MODEL slx_38dcbebacd56
CONFIG AbsTol = auto
CONFIG FixedStep = 0.001
CONFIG MaxStep = auto
CONFIG MinStep = auto
CONFIG PostLoadFcn = , if any(exist('dsrtsu_mdlpostloadfcn', 'file') == [2, 3, 6]), try dsrtsu_mdlpostloadfcn('Execute', bdroot); catch fprintf('Error in PostLoadFcn (dsrtsu_mdlpostloadfcn) for model "%s":\n %s\n', bdroot, lasterr); end, end, 

CONFIG RelTol = 1e-3
CONFIG SampleTimeConstraint = Unconstrained
CONFIG Solver = ode1
CONFIG SolverMode = Auto
CONFIG SolverName = ode1
CONFIG StartTime = 0.0
CONFIG StopTime = Inf
BLOCK [Reference] DS2201ADC_B1  REF=rtilibm/DS2201/DS2201ADC_B1
  BoardNo = 1
  DSProperties = struct('RTI',struct('Version',uint32(1),'BlockType',struct('isSLSource',uint8(1),'isSLSink',uint8(0),'isHWSource',uint8(1),'isHWSink',uint8(0),'isSetup',uint8(0),'isInline',uint8(1),'isNonInline',uint8(0),'isInterrupt',uint8(0),'isChannelwise',uint8(0)),'IOBoardType','DS2201','UnitType','ADC','Identifier','ADCMUX','DialogType','ML','BlockSet','NONE','SlaveProcessor','NONE'))
  Diagnostics = AllowInheritedTsInSrc
  DialogFcn = gui2201adc
  Ports = [0, 5]
  SourceBlock = rtilibm/DS2201/DS2201ADC_B1
  SourceType = DS2201ADC
  UnitName = {'DS2201ADC_B'}
  UnitValues = { 1 }
  channelNo1 = [1 2 3 4]
  channelNo2 = [5 6 7 8]
  channelNo3 = [9 10]
  channelNo4 = -1
  channelNo5 = -1
BLOCK [Reference] DS2201DAC_B1  REF=rtilibm/DS2201/DS2201DAC_B1
  BoardNo = 1
  DSProperties = struct('RTI',struct('Version',uint32(1),'BlockType',struct('isSLSource',uint8(0),'isSLSink',uint8(1),'isHWSource',uint8(0),'isHWSink',uint8(1),'isSetup',uint8(0),'isInline',uint8(1),'isNonInline',uint8(0),'isInterrupt',uint8(0),'isChannelwise',uint8(0)),'IOBoardType','DS2201','UnitType','DAC','Identifier','DAC','DialogType','ML','BlockSet','NONE','SlaveProcessor','NONE'))
  Diagnostics = AllowInheritedTsInSrc
  DialogFcn = gui2201dac
  IOErrorMode = [0 0]
  InitValue = [0 0 0 0 0 0 0 0]
  Ports = [8]
  SourceBlock = rtilibm/DS2201/DS2201DAC_B1
  SourceType = DS2201DAC
  TermMode = [0 0 0 0 0 0 0 0]
  TermValue = [0 0 0 0 0 0 0 0]
  UnitName = {'DS2201DAC_B'}
  UnitValues = { 1 }
BLOCK [Reference] DS2201IN_B3  REF=rtilibm/DS2201/DS2201IN_B1
  BoardNo = 3
  ChannelNos = [1 2 3]
  DSProperties = struct('RTI',struct('Version',uint32(1),'BlockType',struct('isSLSource',uint8(1),'isSLSink',uint8(0),'isHWSource',uint8(1),'isHWSink',uint8(0),'isSetup',uint8(0),'isInline',uint8(1),'isNonInline',uint8(0),'isInterrupt',uint8(0),'isChannelwise',uint8(0)),'IOBoardType','DS2201','UnitType','BIT','Identifier','BITIN','DialogType','ML','BlockSet','NONE','SlaveProcessor','NONE'))
  DialogFcn = gui2201in
  Ports = [0, 1]
  SourceBlock = rtilibm/DS2201/DS2201IN_B1
  SourceType = DS2201IN
  UnitName = { 'DS2201IN_B' }
  UnitValues = { 3 }
BLOCK [DataStoreMemory] Data Store Memory
  DataStoreName = czuj_baz_os_1
  ReadBeforeWriteMsg = warning
  WriteAfterReadMsg = warning
  WriteAfterWriteMsg = warning
BLOCK [DataStoreMemory] Data Store Memory1
  DataStoreName = os2_zad
  ReadBeforeWriteMsg = warning
  WriteAfterReadMsg = warning
  WriteAfterWriteMsg = warning
BLOCK [DataStoreMemory] Data Store Memory10
  DataStoreName = czuj_baz_os_3
  ReadBeforeWriteMsg = warning
  WriteAfterReadMsg = warning
  WriteAfterWriteMsg = warning
BLOCK [DataStoreMemory] Data Store Memory11
  DataStoreName = Bazowanie_on
  OutDataTypeStr = double
  ReadBeforeWriteMsg = warning
  WriteAfterReadMsg = warning
  WriteAfterWriteMsg = warning
BLOCK [DataStoreMemory] Data Store Memory12
  DataStoreName = Bazowanie_off
  OutDataTypeStr = double
  ReadBeforeWriteMsg = warning
  WriteAfterReadMsg = warning
  WriteAfterWriteMsg = warning
BLOCK [DataStoreMemory] Data Store Memory13
  DataStoreName = reset_os_1
  ReadBeforeWriteMsg = warning
  WriteAfterReadMsg = warning
  WriteAfterWriteMsg = warning
BLOCK [DataStoreMemory] Data Store Memory14
  DataStoreName = reset_os_2
  ReadBeforeWriteMsg = warning
  WriteAfterReadMsg = warning
  WriteAfterWriteMsg = warning
BLOCK [DataStoreMemory] Data Store Memory15
  DataStoreName = reset_os_3
  ReadBeforeWriteMsg = warning
  WriteAfterReadMsg = warning
  WriteAfterWriteMsg = warning
BLOCK [DataStoreMemory] Data Store Memory16
  DataStoreName = predkosc_robocza
  ReadBeforeWriteMsg = warning
  WriteAfterReadMsg = warning
  WriteAfterWriteMsg = warning
BLOCK [DataStoreMemory] Data Store Memory17
  DataStoreName = wpolczynnik_predkosci_roboczej
  ReadBeforeWriteMsg = warning
  WriteAfterReadMsg = warning
  WriteAfterWriteMsg = warning
BLOCK [DataStoreMemory] Data Store Memory2
  DataStoreName = os3_zad
  ReadBeforeWriteMsg = warning
  WriteAfterReadMsg = warning
  WriteAfterWriteMsg = warning
BLOCK [DataStoreMemory] Data Store Memory3
  DataStoreName = os4_zad
  ReadBeforeWriteMsg = warning
  WriteAfterReadMsg = warning
  WriteAfterWriteMsg = warning
BLOCK [DataStoreMemory] Data Store Memory4
  DataStoreName = os5_zad
  ReadBeforeWriteMsg = warning
  WriteAfterReadMsg = warning
  WriteAfterWriteMsg = warning
BLOCK [DataStoreMemory] Data Store Memory5
  DataStoreName = os2_panel
  ReadBeforeWriteMsg = warning
  WriteAfterReadMsg = warning
  WriteAfterWriteMsg = warning
BLOCK [DataStoreMemory] Data Store Memory6
  DataStoreName = os3_panel
  ReadBeforeWriteMsg = warning
  WriteAfterReadMsg = warning
  WriteAfterWriteMsg = warning
BLOCK [DataStoreMemory] Data Store Memory7
  DataStoreName = os4_panel
  ReadBeforeWriteMsg = warning
  WriteAfterReadMsg = warning
  WriteAfterWriteMsg = warning
BLOCK [DataStoreMemory] Data Store Memory8
  DataStoreName = os5_panel
  ReadBeforeWriteMsg = warning
  WriteAfterReadMsg = warning
  WriteAfterWriteMsg = warning
BLOCK [DataStoreMemory] Data Store Memory9
  DataStoreName = czuj_baz_os_2
  ReadBeforeWriteMsg = warning
  WriteAfterReadMsg = warning
  WriteAfterWriteMsg = warning
BLOCK [DataStoreRead] Data Store Read
  DataStoreName = os1_zad
  Ports = [0, 1]
BLOCK [DataStoreRead] Data Store Read1
  DataStoreName = os2_zad
  Ports = [0, 1]
BLOCK [DataStoreRead] Data Store Read10
  DataStoreName = czuj_baz_os_1
  Ports = [0, 1]
BLOCK [DataStoreRead] Data Store Read11
  DataStoreName = reset_os_3
  Ports = [0, 1]
BLOCK [DataStoreRead] Data Store Read12
  DataStoreName = Bazowanie_off
  Ports = [0, 1]
BLOCK [DataStoreRead] Data Store Read13
  DataStoreName = reset_os_2
  Ports = [0, 1]
BLOCK [DataStoreRead] Data Store Read14
  DataStoreName = reset_os_1
  Ports = [0, 1]
BLOCK [DataStoreRead] Data Store Read15
  DataStoreName = predkosc_robocza
  Ports = [0, 1]
BLOCK [DataStoreRead] Data Store Read16
  DataStoreName = wpolczynnik_predkosci_roboczej
  Ports = [0, 1]
BLOCK [DataStoreRead] Data Store Read2
  DataStoreName = os3_zad
  Ports = [0, 1]
BLOCK [DataStoreRead] Data Store Read3
  DataStoreName = os4_zad
  Ports = [0, 1]
BLOCK [DataStoreRead] Data Store Read4
  DataStoreName = os5_zad
  Ports = [0, 1]
BLOCK [DataStoreRead] Data Store Read5
  DataStoreName = os1_panel
  Ports = [0, 1]
BLOCK [DataStoreRead] Data Store Read6
  DataStoreName = os2_panel
  Ports = [0, 1]
BLOCK [DataStoreRead] Data Store Read7
  DataStoreName = os3_panel
  Ports = [0, 1]
BLOCK [DataStoreRead] Data Store Read8
  DataStoreName = os4_panel
  Ports = [0, 1]
BLOCK [DataStoreRead] Data Store Read9
  DataStoreName = os5_panel
  Ports = [0, 1]
BLOCK [DataStoreWrite] Data Store Write
  DataStoreName = os1_zad
  Ports = [1]
BLOCK [DataStoreWrite] Data Store Write1
  DataStoreName = os2_zad
  Ports = [1]
BLOCK [DataStoreWrite] Data Store Write2
  DataStoreName = os3_zad
  Ports = [1]
BLOCK [DataStoreWrite] Data Store Write3
  DataStoreName = os4_zad
  Ports = [1]
BLOCK [DataStoreWrite] Data Store Write4
  DataStoreName = os5_zad
  Ports = [1]
BLOCK [DataStoreWrite] Data Store Write5
  DataStoreName = czuj_baz_os_1
  Ports = [1]
BLOCK [DataStoreWrite] Data Store Write6
  DataStoreName = czuj_baz_os_2
  Ports = [1]
BLOCK [DataStoreWrite] Data Store Write7
  DataStoreName = czuj_baz_os_3
  Ports = [1]
BLOCK [DataStoreWrite] Data Store Write8
  DataStoreName = wpolczynnik_predkosci_roboczej
  Ports = [1]
BLOCK [Demux] Demux
  DisplayOption = bar
  Outputs = 2
  Ports = [1, 2]
BLOCK [Demux] Demux1
  DisplayOption = bar
  Outputs = 2
  Ports = [1, 2]
BLOCK [Demux] Demux2
  DisplayOption = bar
  Outputs = 3
  Ports = [1, 3]
BLOCK [From] From
  GotoTag = os1
  TagVisibility = global
BLOCK [From] From1
  GotoTag = os2
  TagVisibility = global
BLOCK [From] From2
  GotoTag = os3
  TagVisibility = global
BLOCK [From] From3
  GotoTag = os4
  TagVisibility = global
BLOCK [From] From4
  GotoTag = os5
  TagVisibility = global
BLOCK [Gain] Gain
  Gain = 0.01
  OutDataTypeStr = Inherit: Inherit via internal rule
  ParamDataTypeStr = Inherit: Inherit via internal rule
  SaturateOnIntegerOverflow = off
BLOCK [Goto] Goto
  GotoTag = os1
  TagVisibility = global
BLOCK [Goto] Goto1
  GotoTag = os2
  TagVisibility = global
BLOCK [Goto] Goto2
  GotoTag = os3
  TagVisibility = global
BLOCK [Goto] Goto3
  GotoTag = os4
  TagVisibility = global
BLOCK [Goto] Goto4
  GotoTag = os5
  TagVisibility = global
BLOCK [Ground] Ground
BLOCK [Ground] Ground1
BLOCK [Ground] Ground2
BLOCK [SubSystem] Moduł sprawdzający czy wpisana pozycja dla ruchu, może być wartością zadaną dla regulatorów P, praz podana na elementy wykonawcze2
  Ports = [5, 5]
  RequestExecContextInheritance = off
BLOCK [Abs] Moduł sprawdzający czy wpisana pozycja dla ruchu, może być wartością zadaną dla regulatorów P, praz podana na elementy wykonawcze2/Abs
  SaturateOnIntegerOverflow = off
BLOCK [Abs] Moduł sprawdzający czy wpisana pozycja dla ruchu, może być wartością zadaną dla regulatorów P, praz podana na elementy wykonawcze2/Abs1
  SaturateOnIntegerOverflow = off
BLOCK [Abs] Moduł sprawdzający czy wpisana pozycja dla ruchu, może być wartością zadaną dla regulatorów P, praz podana na elementy wykonawcze2/Abs2
  SaturateOnIntegerOverflow = off
BLOCK [Constant] Moduł sprawdzający czy wpisana pozycja dla ruchu, może być wartością zadaną dla regulatorów P, praz podana na elementy wykonawcze2/Constant
  Value = 160
BLOCK [Constant] Moduł sprawdzający czy wpisana pozycja dla ruchu, może być wartością zadaną dla regulatorów P, praz podana na elementy wykonawcze2/Constant1
BLOCK [Constant] Moduł sprawdzający czy wpisana pozycja dla ruchu, może być wartością zadaną dla regulatorów P, praz podana na elementy wykonawcze2/Constant10
BLOCK [Constant] Moduł sprawdzający czy wpisana pozycja dla ruchu, może być wartością zadaną dla regulatorów P, praz podana na elementy wykonawcze2/Constant11
BLOCK [Constant] Moduł sprawdzający czy wpisana pozycja dla ruchu, może być wartością zadaną dla regulatorów P, praz podana na elementy wykonawcze2/Constant12
  Value = 25
BLOCK [Constant] Moduł sprawdzający czy wpisana pozycja dla ruchu, może być wartością zadaną dla regulatorów P, praz podana na elementy wykonawcze2/Constant13
BLOCK [Constant] Moduł sprawdzający czy wpisana pozycja dla ruchu, może być wartością zadaną dla regulatorów P, praz podana na elementy wykonawcze2/Constant14
  Value = 0
BLOCK [Constant] Moduł sprawdzający czy wpisana pozycja dla ruchu, może być wartością zadaną dla regulatorów P, praz podana na elementy wykonawcze2/Constant15
  Value = 120
BLOCK [Constant] Moduł sprawdzający czy wpisana pozycja dla ruchu, może być wartością zadaną dla regulatorów P, praz podana na elementy wykonawcze2/Constant16
BLOCK [Constant] Moduł sprawdzający czy wpisana pozycja dla ruchu, może być wartością zadaną dla regulatorów P, praz podana na elementy wykonawcze2/Constant17
  Value = 25
BLOCK [Constant] Moduł sprawdzający czy wpisana pozycja dla ruchu, może być wartością zadaną dla regulatorów P, praz podana na elementy wykonawcze2/Constant18
BLOCK [Constant] Moduł sprawdzający czy wpisana pozycja dla ruchu, może być wartością zadaną dla regulatorów P, praz podana na elementy wykonawcze2/Constant19
  Value = 0
BLOCK [Constant] Moduł sprawdzający czy wpisana pozycja dla ruchu, może być wartością zadaną dla regulatorów P, praz podana na elementy wykonawcze2/Constant2
  Value = 0
BLOCK [Constant] Moduł sprawdzający czy wpisana pozycja dla ruchu, może być wartością zadaną dla regulatorów P, praz podana na elementy wykonawcze2/Constant20
  Value = 150
BLOCK [Constant] Moduł sprawdzający czy wpisana pozycja dla ruchu, może być wartością zadaną dla regulatorów P, praz podana na elementy wykonawcze2/Constant21
  Value = 40
BLOCK [Constant] Moduł sprawdzający czy wpisana pozycja dla ruchu, może być wartością zadaną dla regulatorów P, praz podana na elementy wykonawcze2/Constant22
  Value = 0
BLOCK [Constant] Moduł sprawdzający czy wpisana pozycja dla ruchu, może być wartością zadaną dla regulatorów P, praz podana na elementy wykonawcze2/Constant23
BLOCK [Constant] Moduł sprawdzający czy wpisana pozycja dla ruchu, może być wartością zadaną dla regulatorów P, praz podana na elementy wykonawcze2/Constant3
  Value = 40
BLOCK [Constant] Moduł sprawdzający czy wpisana pozycja dla ruchu, może być wartością zadaną dla regulatorów P, praz podana na elementy wykonawcze2/Constant4
BLOCK [Constant] Moduł sprawdzający czy wpisana pozycja dla ruchu, może być wartością zadaną dla regulatorów P, praz podana na elementy wykonawcze2/Constant5
  Value = 0
BLOCK [Constant] Moduł sprawdzający czy wpisana pozycja dla ruchu, może być wartością zadaną dla regulatorów P, praz podana na elementy wykonawcze2/Constant6
  Value = 25
BLOCK [Constant] Moduł sprawdzający czy wpisana pozycja dla ruchu, może być wartością zadaną dla regulatorów P, praz podana na elementy wykonawcze2/Constant7
BLOCK [Constant] Moduł sprawdzający czy wpisana pozycja dla ruchu, może być wartością zadaną dla regulatorów P, praz podana na elementy wykonawcze2/Constant8
  Value = 0
BLOCK [Constant] Moduł sprawdzający czy wpisana pozycja dla ruchu, może być wartością zadaną dla regulatorów P, praz podana na elementy wykonawcze2/Constant9
  Value = 40
BLOCK [DataStoreRead] Moduł sprawdzający czy wpisana pozycja dla ruchu, może być wartością zadaną dla regulatorów P, praz podana na elementy wykonawcze2/Data Store Read17
  DataStoreName = os1_zad
  Ports = [0, 1]
BLOCK [DataStoreRead] Moduł sprawdzający czy wpisana pozycja dla ruchu, może być wartością zadaną dla regulatorów P, praz podana na elementy wykonawcze2/Data Store Read18
  DataStoreName = os2_zad
  Ports = [0, 1]
BLOCK [DataStoreRead] Moduł sprawdzający czy wpisana pozycja dla ruchu, może być wartością zadaną dla regulatorów P, praz podana na elementy wykonawcze2/Data Store Read19
  DataStoreName = os3_zad
  Ports = [0, 1]
BLOCK [DataStoreRead] Moduł sprawdzający czy wpisana pozycja dla ruchu, może być wartością zadaną dla regulatorów P, praz podana na elementy wykonawcze2/Data Store Read20
  DataStoreName = os4_zad
  Ports = [0, 1]
BLOCK [DataStoreRead] Moduł sprawdzający czy wpisana pozycja dla ruchu, może być wartością zadaną dla regulatorów P, praz podana na elementy wykonawcze2/Data Store Read21
  DataStoreName = os5_zad
  Ports = [0, 1]
BLOCK [From] Moduł sprawdzający czy wpisana pozycja dla ruchu, może być wartością zadaną dla regulatorów P, praz podana na elementy wykonawcze2/From
  GotoTag = os_3_wpis
  TagVisibility = global
BLOCK [From] Moduł sprawdzający czy wpisana pozycja dla ruchu, może być wartością zadaną dla regulatorów P, praz podana na elementy wykonawcze2/From1
  GotoTag = os_2_wpis
  TagVisibility = global
BLOCK [From] Moduł sprawdzający czy wpisana pozycja dla ruchu, może być wartością zadaną dla regulatorów P, praz podana na elementy wykonawcze2/From2
  GotoTag = os_5_wpis
  TagVisibility = global
BLOCK [From] Moduł sprawdzający czy wpisana pozycja dla ruchu, może być wartością zadaną dla regulatorów P, praz podana na elementy wykonawcze2/From3
  GotoTag = os_2_wpis
  TagVisibility = global
BLOCK [From] Moduł sprawdzający czy wpisana pozycja dla ruchu, może być wartością zadaną dla regulatorów P, praz podana na elementy wykonawcze2/From4
  GotoTag = os_1_wpis
  TagVisibility = global
BLOCK [From] Moduł sprawdzający czy wpisana pozycja dla ruchu, może być wartością zadaną dla regulatorów P, praz podana na elementy wykonawcze2/From5
  GotoTag = os_4_wpis
  TagVisibility = global
BLOCK [From] Moduł sprawdzający czy wpisana pozycja dla ruchu, może być wartością zadaną dla regulatorów P, praz podana na elementy wykonawcze2/From6
  GotoTag = os_3_wpis
  TagVisibility = global
BLOCK [Goto] Moduł sprawdzający czy wpisana pozycja dla ruchu, może być wartością zadaną dla regulatorów P, praz podana na elementy wykonawcze2/Goto
  GotoTag = os_1_wpis
  TagVisibility = global
BLOCK [Goto] Moduł sprawdzający czy wpisana pozycja dla ruchu, może być wartością zadaną dla regulatorów P, praz podana na elementy wykonawcze2/Goto1
  GotoTag = os_2_wpis
  TagVisibility = global
BLOCK [Goto] Moduł sprawdzający czy wpisana pozycja dla ruchu, może być wartością zadaną dla regulatorów P, praz podana na elementy wykonawcze2/Goto2
  GotoTag = os_5_wpis
  TagVisibility = global
BLOCK [Goto] Moduł sprawdzający czy wpisana pozycja dla ruchu, może być wartością zadaną dla regulatorów P, praz podana na elementy wykonawcze2/Goto3
  GotoTag = os_3_wpis
  TagVisibility = global
BLOCK [Goto] Moduł sprawdzający czy wpisana pozycja dla ruchu, może być wartością zadaną dla regulatorów P, praz podana na elementy wykonawcze2/Goto4
  GotoTag = os_4_wpis
  TagVisibility = global
BLOCK [Logic] Moduł sprawdzający czy wpisana pozycja dla ruchu, może być wartością zadaną dla regulatorów P, praz podana na elementy wykonawcze2/Logical Operator
  AllPortsSameDT = off
  Ports = [2, 1]
BLOCK [Logic] Moduł sprawdzający czy wpisana pozycja dla ruchu, może być wartością zadaną dla regulatorów P, praz podana na elementy wykonawcze2/Logical Operator1
  AllPortsSameDT = off
  Ports = [2, 1]
BLOCK [Logic] Moduł sprawdzający czy wpisana pozycja dla ruchu, może być wartością zadaną dla regulatorów P, praz podana na elementy wykonawcze2/Logical Operator2
  AllPortsSameDT = off
  Ports = [2, 1]
BLOCK [Logic] Moduł sprawdzający czy wpisana pozycja dla ruchu, może być wartością zadaną dla regulatorów P, praz podana na elementy wykonawcze2/Logical Operator3
  AllPortsSameDT = off
  Inputs = 6
  Ports = [6, 1]
BLOCK [Sum] Moduł sprawdzający czy wpisana pozycja dla ruchu, może być wartością zadaną dla regulatorów P, praz podana na elementy wykonawcze2/Sum
  IconShape = round
  InputSameDT = off
  Inputs = |+-
  OutDataTypeStr = Inherit: Inherit via internal rule
  Ports = [2, 1]
  SaturateOnIntegerOverflow = off
BLOCK [Sum] Moduł sprawdzający czy wpisana pozycja dla ruchu, może być wartością zadaną dla regulatorów P, praz podana na elementy wykonawcze2/Sum1
  IconShape = round
  InputSameDT = off
  Inputs = |+-
  OutDataTypeStr = Inherit: Inherit via internal rule
  Ports = [2, 1]
  SaturateOnIntegerOverflow = off
BLOCK [Sum] Moduł sprawdzający czy wpisana pozycja dla ruchu, może być wartością zadaną dla regulatorów P, praz podana na elementy wykonawcze2/Sum2
  IconShape = round
  InputSameDT = off
  Inputs = |++
  OutDataTypeStr = Inherit: Inherit via internal rule
  Ports = [2, 1]
  SaturateOnIntegerOverflow = off
BLOCK [Sum] Moduł sprawdzający czy wpisana pozycja dla ruchu, może być wartością zadaną dla regulatorów P, praz podana na elementy wykonawcze2/Sum3
  IconShape = round
  InputSameDT = off
  Inputs = |+-
  OutDataTypeStr = Inherit: Inherit via internal rule
  Ports = [2, 1]
  SaturateOnIntegerOverflow = off
BLOCK [Sum] Moduł sprawdzający czy wpisana pozycja dla ruchu, może być wartością zadaną dla regulatorów P, praz podana na elementy wykonawcze2/Sum4
  IconShape = round
  InputSameDT = off
  Inputs = |++
  OutDataTypeStr = Inherit: Inherit via internal rule
  Ports = [2, 1]
  SaturateOnIntegerOverflow = off
BLOCK [Sum] Moduł sprawdzający czy wpisana pozycja dla ruchu, może być wartością zadaną dla regulatorów P, praz podana na elementy wykonawcze2/Sum5
  IconShape = round
  InputSameDT = off
  Inputs = |+-
  OutDataTypeStr = Inherit: Inherit via internal rule
  Ports = [2, 1]
  SaturateOnIntegerOverflow = off
BLOCK [Sum] Moduł sprawdzający czy wpisana pozycja dla ruchu, może być wartością zadaną dla regulatorów P, praz podana na elementy wykonawcze2/Sum6
  IconShape = round
  InputSameDT = off
  Inputs = |++
  OutDataTypeStr = Inherit: Inherit via internal rule
  Ports = [2, 1]
  SaturateOnIntegerOverflow = off
BLOCK [Sum] Moduł sprawdzający czy wpisana pozycja dla ruchu, może być wartością zadaną dla regulatorów P, praz podana na elementy wykonawcze2/Sum7
  IconShape = round
  InputSameDT = off
  Inputs = |+-
  OutDataTypeStr = Inherit: Inherit via internal rule
  Ports = [2, 1]
  SaturateOnIntegerOverflow = off
BLOCK [Sum] Moduł sprawdzający czy wpisana pozycja dla ruchu, może być wartością zadaną dla regulatorów P, praz podana na elementy wykonawcze2/Sum8
  IconShape = round
  InputSameDT = off
  Inputs = |+-
  OutDataTypeStr = Inherit: Inherit via internal rule
  Ports = [2, 1]
  SaturateOnIntegerOverflow = off
BLOCK [Sum] Moduł sprawdzający czy wpisana pozycja dla ruchu, może być wartością zadaną dla regulatorów P, praz podana na elementy wykonawcze2/Sum9
  IconShape = round
  InputSameDT = off
  Inputs = |+-
  OutDataTypeStr = Inherit: Inherit via internal rule
  Ports = [2, 1]
  SaturateOnIntegerOverflow = off
BLOCK [Switch] Moduł sprawdzający czy wpisana pozycja dla ruchu, może być wartością zadaną dla regulatorów P, praz podana na elementy wykonawcze2/Switch
  InputSameDT = off
  SaturateOnIntegerOverflow = off
BLOCK [Switch] Moduł sprawdzający czy wpisana pozycja dla ruchu, może być wartością zadaną dla regulatorów P, praz podana na elementy wykonawcze2/Switch1
  InputSameDT = off
  SaturateOnIntegerOverflow = off
BLOCK [Switch] Moduł sprawdzający czy wpisana pozycja dla ruchu, może być wartością zadaną dla regulatorów P, praz podana na elementy wykonawcze2/Switch10
  Criteria = u2 > Threshold
  InputSameDT = off
  SaturateOnIntegerOverflow = off
BLOCK [Switch] Moduł sprawdzający czy wpisana pozycja dla ruchu, może być wartością zadaną dla regulatorów P, praz podana na elementy wykonawcze2/Switch11
  Criteria = u2 > Threshold
  InputSameDT = off
  SaturateOnIntegerOverflow = off
BLOCK [Switch] Moduł sprawdzający czy wpisana pozycja dla ruchu, może być wartością zadaną dla regulatorów P, praz podana na elementy wykonawcze2/Switch12
  Criteria = u2 > Threshold
  InputSameDT = off
  SaturateOnIntegerOverflow = off
BLOCK [Switch] Moduł sprawdzający czy wpisana pozycja dla ruchu, może być wartością zadaną dla regulatorów P, praz podana na elementy wykonawcze2/Switch13
  Criteria = u2 > Threshold
  InputSameDT = off
  SaturateOnIntegerOverflow = off
BLOCK [Switch] Moduł sprawdzający czy wpisana pozycja dla ruchu, może być wartością zadaną dla regulatorów P, praz podana na elementy wykonawcze2/Switch2
  InputSameDT = off
  SaturateOnIntegerOverflow = off
BLOCK [Switch] Moduł sprawdzający czy wpisana pozycja dla ruchu, może być wartością zadaną dla regulatorów P, praz podana na elementy wykonawcze2/Switch3
  InputSameDT = off
  SaturateOnIntegerOverflow = off
BLOCK [Switch] Moduł sprawdzający czy wpisana pozycja dla ruchu, może być wartością zadaną dla regulatorów P, praz podana na elementy wykonawcze2/Switch4
  InputSameDT = off
  SaturateOnIntegerOverflow = off
BLOCK [Switch] Moduł sprawdzający czy wpisana pozycja dla ruchu, może być wartością zadaną dla regulatorów P, praz podana na elementy wykonawcze2/Switch5
  InputSameDT = off
  SaturateOnIntegerOverflow = off
BLOCK [Switch] Moduł sprawdzający czy wpisana pozycja dla ruchu, może być wartością zadaną dla regulatorów P, praz podana na elementy wykonawcze2/Switch6
  InputSameDT = off
  SaturateOnIntegerOverflow = off
BLOCK [Switch] Moduł sprawdzający czy wpisana pozycja dla ruchu, może być wartością zadaną dla regulatorów P, praz podana na elementy wykonawcze2/Switch7
  InputSameDT = off
  SaturateOnIntegerOverflow = off
BLOCK [Switch] Moduł sprawdzający czy wpisana pozycja dla ruchu, może być wartością zadaną dla regulatorów P, praz podana na elementy wykonawcze2/Switch8
  InputSameDT = off
  SaturateOnIntegerOverflow = off
BLOCK [Switch] Moduł sprawdzający czy wpisana pozycja dla ruchu, może być wartością zadaną dla regulatorów P, praz podana na elementy wykonawcze2/Switch9
  Criteria = u2 > Threshold
  InputSameDT = off
  SaturateOnIntegerOverflow = off
BLOCK [Inport] Moduł sprawdzający czy wpisana pozycja dla ruchu, może być wartością zadaną dla regulatorów P, praz podana na elementy wykonawcze2/os1_
  IconDisplay = Port number
BLOCK [Inport] Moduł sprawdzający czy wpisana pozycja dla ruchu, może być wartością zadaną dla regulatorów P, praz podana na elementy wykonawcze2/os2
  IconDisplay = Port number
  Port = 2
BLOCK [Inport] Moduł sprawdzający czy wpisana pozycja dla ruchu, może być wartością zadaną dla regulatorów P, praz podana na elementy wykonawcze2/os3
  IconDisplay = Port number
  Port = 3
BLOCK [Inport] Moduł sprawdzający czy wpisana pozycja dla ruchu, może być wartością zadaną dla regulatorów P, praz podana na elementy wykonawcze2/os4
  IconDisplay = Port number
  Port = 4
BLOCK [Inport] Moduł sprawdzający czy wpisana pozycja dla ruchu, może być wartością zadaną dla regulatorów P, praz podana na elementy wykonawcze2/os5
  IconDisplay = Port number
  Port = 5
BLOCK [Outport] Moduł sprawdzający czy wpisana pozycja dla ruchu, może być wartością zadaną dla regulatorów P, praz podana na elementy wykonawcze2/os_1
  IconDisplay = Port number
BLOCK [Outport] Moduł sprawdzający czy wpisana pozycja dla ruchu, może być wartością zadaną dla regulatorów P, praz podana na elementy wykonawcze2/os_2
  IconDisplay = Port number
  Port = 2
BLOCK [Outport] Moduł sprawdzający czy wpisana pozycja dla ruchu, może być wartością zadaną dla regulatorów P, praz podana na elementy wykonawcze2/os_3
  IconDisplay = Port number
  Port = 3
BLOCK [Outport] Moduł sprawdzający czy wpisana pozycja dla ruchu, może być wartością zadaną dla regulatorów P, praz podana na elementy wykonawcze2/os_4
  IconDisplay = Port number
  Port = 4
BLOCK [Outport] Moduł sprawdzający czy wpisana pozycja dla ruchu, może być wartością zadaną dla regulatorów P, praz podana na elementy wykonawcze2/os_5
  IconDisplay = Port number
  Port = 5
BLOCK [SubSystem] Position 1
  Ports = [2, 1]
  RequestExecContextInheritance = off
BLOCK [SubSystem] Position 1/Filters 1
  Ports = [1, 2]
  RequestExecContextInheritance = off
  ShowPortLabels = none
BLOCK [SubSystem] Position 1/Filters 1/Analog Butterworth LP Filter
  Ports = [1, 1]
  RequestExecContextInheritance = off
BLOCK [ZeroPole] Position 1/Filters 1/Analog Butterworth LP Filter/Analog Butterworth LP Filter
  Gain = k
  Poles = p
  Zeros = z
BLOCK [Inport] Position 1/Filters 1/Analog Butterworth LP Filter/In1
  IconDisplay = Port number
BLOCK [Outport] Position 1/Filters 1/Analog Butterworth LP Filter/Out1
  IconDisplay = Port number
BLOCK [SubSystem] Position 1/Filters 1/Analog Butterworth LP Filter1
  Ports = [1, 1]
  RequestExecContextInheritance = off
BLOCK [ZeroPole] Position 1/Filters 1/Analog Butterworth LP Filter1/Analog Butterworth LP Filter1
  Gain = k
  Poles = p
  Zeros = z
BLOCK [Inport] Position 1/Filters 1/Analog Butterworth LP Filter1/In1
  IconDisplay = Port number
BLOCK [Outport] Position 1/Filters 1/Analog Butterworth LP Filter1/Out1
  IconDisplay = Port number
BLOCK [Outport] Position 1/Filters 1/Cos
  IconDisplay = Port number
  Port = 2
BLOCK [Demux] Position 1/Filters 1/Demux
  Outputs = 2
  Ports = [1, 2]
BLOCK [Outport] Position 1/Filters 1/Sin
  IconDisplay = Port number
BLOCK [Inport] Position 1/Filters 1/Sin && Cos
  IconDisplay = Port number
BLOCK [Outport] Position 1/Out1
  IconDisplay = Port number
BLOCK [SubSystem] Position 1/Position Calculation 1
  Ports = [3, 1]
  RequestExecContextInheritance = off
  ShowPortLabels = none
BLOCK [Fcn] Position 1/Position Calculation 1/Atan2
  Expr = atan2(u[1],u[2])
BLOCK [Gain] Position 1/Position Calculation 1/Conversion Rad to Deg
  Gain = 180/pi
BLOCK [Gain] Position 1/Position Calculation 1/Conversion Rotation to Angle
  Gain = 2*pi
BLOCK [Inport] Position 1/Position Calculation 1/Cos
  IconDisplay = Port number
  Port = 2
BLOCK [DeadZone] Position 1/Position Calculation 1/Dead Zone
  LowerValue = -5000
  UpperValue = 5000
BLOCK [Derivative] Position 1/Position Calculation 1/Derivative
BLOCK [Gain] Position 1/Position Calculation 1/Gear
  Gain = 6.33e-3
BLOCK [Switch] Position 1/Position Calculation 1/Init Angle
  Threshold = 1
BLOCK [Memory] Position 1/Position Calculation 1/Memory
BLOCK [Memory] Position 1/Position Calculation 1/Memory1
BLOCK [Mux] Position 1/Position Calculation 1/Mux
  Inputs = 2
  Ports = [2, 1]
BLOCK [Outport] Position 1/Position Calculation 1/Position
  IconDisplay = Port number
BLOCK [Product] Position 1/Position Calculation 1/Product
  Ports = [2, 1]
BLOCK [Inport] Position 1/Position Calculation 1/Reset (Impulse)
  IconDisplay = Port number
  Port = 3
BLOCK [Saturate] Position 1/Position Calculation 1/Saturation
  InputPortMap = u0
  LowerLimit = -1
  Ports = [1, 1]
  UpperLimit = 1
BLOCK [Inport] Position 1/Position Calculation 1/Sin
  IconDisplay = Port number
BLOCK [Sum] Position 1/Position Calculation 1/Sum
  Inputs = +-
  Ports = [2, 1]
BLOCK [Sum] Position 1/Position Calculation 1/Sum1
  Inputs = ++-
  Ports = [3, 1]
BLOCK [Inport] Position 1/Reset 1
  IconDisplay = Port number
  Port = 2
BLOCK [Inport] Position 1/Sin && Cos1
  IconDisplay = Port number
BLOCK [SubSystem] Position 2
  Ports = [2, 1]
  RequestExecContextInheritance = off
BLOCK [SubSystem] Position 2/Filters 2
  Ports = [1, 2]
  RequestExecContextInheritance = off
  ShowPortLabels = none
BLOCK [SubSystem] Position 2/Filters 2/Analog Butterworth LP Filter
  Ports = [1, 1]
  RequestExecContextInheritance = off
BLOCK [ZeroPole] Position 2/Filters 2/Analog Butterworth LP Filter/Analog Butterworth LP Filter
  Gain = k
  Poles = p
  Zeros = z
BLOCK [Inport] Position 2/Filters 2/Analog Butterworth LP Filter/In1
  IconDisplay = Port number
BLOCK [Outport] Position 2/Filters 2/Analog Butterworth LP Filter/Out1
  IconDisplay = Port number
BLOCK [SubSystem] Position 2/Filters 2/Analog Butterworth LP Filter1
  Ports = [1, 1]
  RequestExecContextInheritance = off
BLOCK [ZeroPole] Position 2/Filters 2/Analog Butterworth LP Filter1/Analog Butterworth LP Filter1
  Gain = k
  Poles = p
  Zeros = z
BLOCK [Inport] Position 2/Filters 2/Analog Butterworth LP Filter1/In1
  IconDisplay = Port number
BLOCK [Outport] Position 2/Filters 2/Analog Butterworth LP Filter1/Out1
  IconDisplay = Port number
BLOCK [Outport] Position 2/Filters 2/Cos
  IconDisplay = Port number
  Port = 2
BLOCK [Demux] Position 2/Filters 2/Demux
  Outputs = 2
  Ports = [1, 2]
BLOCK [Outport] Position 2/Filters 2/Sin
  IconDisplay = Port number
BLOCK [Inport] Position 2/Filters 2/Sin && Cos
  IconDisplay = Port number
BLOCK [Outport] Position 2/Out1
  IconDisplay = Port number
BLOCK [SubSystem] Position 2/Position Calculation 2
  Ports = [3, 1]
  RequestExecContextInheritance = off
  ShowPortLabels = none
BLOCK [Fcn] Position 2/Position Calculation 2/Atan2
  Expr = atan2(u[1],u[2])
BLOCK [Gain] Position 2/Position Calculation 2/Conversion Rad to Deg
  Gain = 180/pi
BLOCK [Gain] Position 2/Position Calculation 2/Conversion Rotation to Angle
  Gain = 2*pi
BLOCK [Inport] Position 2/Position Calculation 2/Cos
  IconDisplay = Port number
  Port = 2
BLOCK [DeadZone] Position 2/Position Calculation 2/Dead Zone
  LowerValue = -5000
  UpperValue = 5000
BLOCK [Derivative] Position 2/Position Calculation 2/Derivative
BLOCK [Gain] Position 2/Position Calculation 2/Gear
  Gain = 6.37e-3
BLOCK [Switch] Position 2/Position Calculation 2/Init Angle
  Threshold = 1
BLOCK [Memory] Position 2/Position Calculation 2/Memory
BLOCK [Memory] Position 2/Position Calculation 2/Memory1
BLOCK [Mux] Position 2/Position Calculation 2/Mux
  Inputs = 2
  Ports = [2, 1]
BLOCK [Outport] Position 2/Position Calculation 2/Position
  IconDisplay = Port number
BLOCK [Product] Position 2/Position Calculation 2/Product
  Ports = [2, 1]
BLOCK [Inport] Position 2/Position Calculation 2/Reset (Impulse)
  IconDisplay = Port number
  Port = 3
BLOCK [Saturate] Position 2/Position Calculation 2/Saturation
  InputPortMap = u0
  LowerLimit = -1
  Ports = [1, 1]
  UpperLimit = 1
BLOCK [Inport] Position 2/Position Calculation 2/Sin
  IconDisplay = Port number
BLOCK [Sum] Position 2/Position Calculation 2/Sum
  Inputs = +-
  Ports = [2, 1]
BLOCK [Sum] Position 2/Position Calculation 2/Sum1
  Inputs = ++-
  Ports = [3, 1]
BLOCK [Inport] Position 2/Reset 2
  IconDisplay = Port number
  Port = 2
BLOCK [Inport] Position 2/Sin && Cos2
  IconDisplay = Port number
BLOCK [SubSystem] Position 3
  Ports = [2, 1]
  RequestExecContextInheritance = off
BLOCK [SubSystem] Position 3/Filters 3
  Ports = [1, 2]
  RequestExecContextInheritance = off
  ShowPortLabels = none
BLOCK [SubSystem] Position 3/Filters 3/Analog Butterworth LP Filter
  Ports = [1, 1]
  RequestExecContextInheritance = off
BLOCK [ZeroPole] Position 3/Filters 3/Analog Butterworth LP Filter/Analog Butterworth LP Filter
  Gain = k
  Poles = p
  Zeros = z
BLOCK [Inport] Position 3/Filters 3/Analog Butterworth LP Filter/In1
  IconDisplay = Port number
BLOCK [Outport] Position 3/Filters 3/Analog Butterworth LP Filter/Out1
  IconDisplay = Port number
BLOCK [SubSystem] Position 3/Filters 3/Analog Butterworth LP Filter1
  Ports = [1, 1]
  RequestExecContextInheritance = off
BLOCK [ZeroPole] Position 3/Filters 3/Analog Butterworth LP Filter1/Analog Butterworth LP Filter1
  Gain = k
  Poles = p
  Zeros = z
BLOCK [Inport] Position 3/Filters 3/Analog Butterworth LP Filter1/In1
  IconDisplay = Port number
BLOCK [Outport] Position 3/Filters 3/Analog Butterworth LP Filter1/Out1
  IconDisplay = Port number
BLOCK [Outport] Position 3/Filters 3/Cos
  IconDisplay = Port number
  Port = 2
BLOCK [Demux] Position 3/Filters 3/Demux
  Outputs = 2
  Ports = [1, 2]
BLOCK [Outport] Position 3/Filters 3/Sin
  IconDisplay = Port number
BLOCK [Inport] Position 3/Filters 3/Sin && Cos
  IconDisplay = Port number
BLOCK [Outport] Position 3/Out1
  IconDisplay = Port number
BLOCK [SubSystem] Position 3/Position Calculation 3
  Ports = [3, 1]
  RequestExecContextInheritance = off
  ShowPortLabels = none
BLOCK [Fcn] Position 3/Position Calculation 3/Atan2
  Expr = atan2(u[1],u[2])
BLOCK [Gain] Position 3/Position Calculation 3/Conversion Rad to Deg
  Gain = 180/pi
BLOCK [Gain] Position 3/Position Calculation 3/Conversion Rotation to Angle
  Gain = 2*pi
BLOCK [Inport] Position 3/Position Calculation 3/Cos
  IconDisplay = Port number
  Port = 2
BLOCK [DeadZone] Position 3/Position Calculation 3/Dead Zone
  LowerValue = -5000
  UpperValue = 5000
BLOCK [Derivative] Position 3/Position Calculation 3/Derivative
BLOCK [Gain] Position 3/Position Calculation 3/Gear
  Gain = 6.33e-3
BLOCK [Switch] Position 3/Position Calculation 3/Init Angle
  Threshold = 1
BLOCK [Memory] Position 3/Position Calculation 3/Memory
BLOCK [Memory] Position 3/Position Calculation 3/Memory1
BLOCK [Mux] Position 3/Position Calculation 3/Mux
  Inputs = 2
  Ports = [2, 1]
BLOCK [Outport] Position 3/Position Calculation 3/Position
  IconDisplay = Port number
BLOCK [Product] Position 3/Position Calculation 3/Product
  Ports = [2, 1]
BLOCK [Inport] Position 3/Position Calculation 3/Reset (Impulse)
  IconDisplay = Port number
  Port = 3
BLOCK [Saturate] Position 3/Position Calculation 3/Saturation
  InputPortMap = u0
  LowerLimit = -1
  Ports = [1, 1]
  UpperLimit = 1
BLOCK [Inport] Position 3/Position Calculation 3/Sin
  IconDisplay = Port number
BLOCK [Sum] Position 3/Position Calculation 3/Sum
  Inputs = +-
  Ports = [2, 1]
BLOCK [Sum] Position 3/Position Calculation 3/Sum1
  Inputs = ++-
  Ports = [3, 1]
BLOCK [Inport] Position 3/Reset 3
  IconDisplay = Port number
  Port = 2
BLOCK [Inport] Position 3/Sin && Cos3
  IconDisplay = Port number
BLOCK [SubSystem] Position 4
  Ports = [2, 1]
  RequestExecContextInheritance = off
BLOCK [SubSystem] Position 4/Filters 4
  Ports = [1, 2]
  RequestExecContextInheritance = off
  ShowPortLabels = none
BLOCK [SubSystem] Position 4/Filters 4/Analog Butterworth LP Filter
  Ports = [1, 1]
  RequestExecContextInheritance = off
BLOCK [ZeroPole] Position 4/Filters 4/Analog Butterworth LP Filter/Analog Butterworth LP Filter
  Gain = k
  Poles = p
  Zeros = z
BLOCK [Inport] Position 4/Filters 4/Analog Butterworth LP Filter/In1
  IconDisplay = Port number
BLOCK [Outport] Position 4/Filters 4/Analog Butterworth LP Filter/Out1
  IconDisplay = Port number
BLOCK [SubSystem] Position 4/Filters 4/Analog Butterworth LP Filter1
  Ports = [1, 1]
  RequestExecContextInheritance = off
BLOCK [ZeroPole] Position 4/Filters 4/Analog Butterworth LP Filter1/Analog Butterworth LP Filter1
  Gain = k
  Poles = p
  Zeros = z
BLOCK [Inport] Position 4/Filters 4/Analog Butterworth LP Filter1/In1
  IconDisplay = Port number
BLOCK [Outport] Position 4/Filters 4/Analog Butterworth LP Filter1/Out1
  IconDisplay = Port number
BLOCK [Outport] Position 4/Filters 4/Cos
  IconDisplay = Port number
  Port = 2
BLOCK [Demux] Position 4/Filters 4/Demux
  Outputs = 2
  Ports = [1, 2]
BLOCK [Outport] Position 4/Filters 4/Sin
  IconDisplay = Port number
BLOCK [Inport] Position 4/Filters 4/Sin && Cos
  IconDisplay = Port number
BLOCK [Outport] Position 4/Out1
  IconDisplay = Port number
BLOCK [SubSystem] Position 4/Position Calculation 4
  Ports = [3, 1]
  RequestExecContextInheritance = off
  ShowPortLabels = none
BLOCK [Fcn] Position 4/Position Calculation 4/Atan2
  Expr = atan2(u[1],u[2])
BLOCK [Gain] Position 4/Position Calculation 4/Conversion Rad to Deg
  Gain = 180/pi
BLOCK [Gain] Position 4/Position Calculation 4/Conversion Rotation to Angle
  Gain = 2*pi
BLOCK [Inport] Position 4/Position Calculation 4/Cos
  IconDisplay = Port number
  Port = 2
BLOCK [DeadZone] Position 4/Position Calculation 4/Dead Zone
  LowerValue = -5000
  UpperValue = 5000
BLOCK [Derivative] Position 4/Position Calculation 4/Derivative
BLOCK [Gain] Position 4/Position Calculation 4/Gear
  Gain = 7.87e-3
BLOCK [Switch] Position 4/Position Calculation 4/Init Angle
  Threshold = 1
BLOCK [Memory] Position 4/Position Calculation 4/Memory
BLOCK [Memory] Position 4/Position Calculation 4/Memory1
BLOCK [Mux] Position 4/Position Calculation 4/Mux
  Inputs = 2
  Ports = [2, 1]
BLOCK [Outport] Position 4/Position Calculation 4/Position
  IconDisplay = Port number
BLOCK [Product] Position 4/Position Calculation 4/Product
  Ports = [2, 1]
BLOCK [Inport] Position 4/Position Calculation 4/Reset (Impulse)
  IconDisplay = Port number
  Port = 3
BLOCK [Saturate] Position 4/Position Calculation 4/Saturation
  InputPortMap = u0
  LowerLimit = -1
  Ports = [1, 1]
  UpperLimit = 1
BLOCK [Inport] Position 4/Position Calculation 4/Sin
  IconDisplay = Port number
BLOCK [Sum] Position 4/Position Calculation 4/Sum
  Inputs = +-
  Ports = [2, 1]
BLOCK [Sum] Position 4/Position Calculation 4/Sum1
  Inputs = ++-
  Ports = [3, 1]
BLOCK [Inport] Position 4/Reset 4
  IconDisplay = Port number
  Port = 2
BLOCK [Inport] Position 4/Sin && Cos4
  IconDisplay = Port number
BLOCK [SubSystem] Position 5
  Ports = [2, 1]
  RequestExecContextInheritance = off
BLOCK [SubSystem] Position 5/Filters 5
  Ports = [1, 2]
  RequestExecContextInheritance = off
  ShowPortLabels = none
BLOCK [SubSystem] Position 5/Filters 5/Analog Butterworth LP Filter
  Ports = [1, 1]
  RequestExecContextInheritance = off
BLOCK [ZeroPole] Position 5/Filters 5/Analog Butterworth LP Filter/Analog Butterworth LP Filter
  Gain = k
  Poles = p
  Zeros = z
BLOCK [Inport] Position 5/Filters 5/Analog Butterworth LP Filter/In1
  IconDisplay = Port number
BLOCK [Outport] Position 5/Filters 5/Analog Butterworth LP Filter/Out1
  IconDisplay = Port number
BLOCK [SubSystem] Position 5/Filters 5/Analog Butterworth LP Filter1
  Ports = [1, 1]
  RequestExecContextInheritance = off
BLOCK [ZeroPole] Position 5/Filters 5/Analog Butterworth LP Filter1/Analog Butterworth LP Filter1
  Gain = k
  Poles = p
  Zeros = z
BLOCK [Inport] Position 5/Filters 5/Analog Butterworth LP Filter1/In1
  IconDisplay = Port number
BLOCK [Outport] Position 5/Filters 5/Analog Butterworth LP Filter1/Out1
  IconDisplay = Port number
BLOCK [Outport] Position 5/Filters 5/Cos
  IconDisplay = Port number
  Port = 2
BLOCK [Demux] Position 5/Filters 5/Demux
  Outputs = 2
  Ports = [1, 2]
BLOCK [Outport] Position 5/Filters 5/Sin
  IconDisplay = Port number
BLOCK [Inport] Position 5/Filters 5/Sin && Cos
  IconDisplay = Port number
BLOCK [Outport] Position 5/Out1
  IconDisplay = Port number
BLOCK [SubSystem] Position 5/Position Calculation 5
  Ports = [3, 1]
  RequestExecContextInheritance = off
  ShowPortLabels = none
BLOCK [Fcn] Position 5/Position Calculation 5/Atan2
  Expr = atan2(u[1],u[2])
BLOCK [Gain] Position 5/Position Calculation 5/Conversion Rad to Deg
  Gain = 180/pi
BLOCK [Gain] Position 5/Position Calculation 5/Conversion Rotation to Angle
  Gain = 2*pi
BLOCK [Inport] Position 5/Position Calculation 5/Cos
  IconDisplay = Port number
  Port = 2
BLOCK [DeadZone] Position 5/Position Calculation 5/Dead Zone
  LowerValue = -5000
  UpperValue = 5000
BLOCK [Derivative] Position 5/Position Calculation 5/Derivative
BLOCK [Gain] Position 5/Position Calculation 5/Gear
  Gain = 1.32e-2
BLOCK [Switch] Position 5/Position Calculation 5/Init Angle
  Threshold = 1
BLOCK [Memory] Position 5/Position Calculation 5/Memory
BLOCK [Memory] Position 5/Position Calculation 5/Memory1
BLOCK [Mux] Position 5/Position Calculation 5/Mux
  Inputs = 2
  Ports = [2, 1]
BLOCK [Outport] Position 5/Position Calculation 5/Position
  IconDisplay = Port number
BLOCK [Product] Position 5/Position Calculation 5/Product
  Ports = [2, 1]
BLOCK [Inport] Position 5/Position Calculation 5/Reset (Impulse)
  IconDisplay = Port number
  Port = 3
BLOCK [Saturate] Position 5/Position Calculation 5/Saturation
  InputPortMap = u0
  LowerLimit = -1
  Ports = [1, 1]
  UpperLimit = 1
BLOCK [Inport] Position 5/Position Calculation 5/Sin
  IconDisplay = Port number
BLOCK [Sum] Position 5/Position Calculation 5/Sum
  Inputs = +-
  Ports = [2, 1]
BLOCK [Sum] Position 5/Position Calculation 5/Sum1
  Inputs = ++-
  Ports = [3, 1]
BLOCK [Inport] Position 5/Reset 5
  IconDisplay = Port number
  Port = 2
BLOCK [Inport] Position 5/Sin && Cos5
  IconDisplay = Port number
BLOCK [SubSystem] RTI Data
  CopyFcn = if exist('rtidc'), try,  rtidc('DataHostBlockClbCopy', gcbh); catch, disp(['Warning: ''CopyFcn'' for RTI Data block failed: ' lasterr]); end, end,
  DeleteFcn = if exist('rtidc'), try,  rtidc('DataHostBlockClbDelete', gcbh); catch, disp(['Warning: ''DeleteFcn'' for RTI Data block failed: ' lasterr]); end, end,
  LoadFcn = if exist('rtidc'), try,  rtidc('DataHostBlockClbLoad', gcbh); catch, disp(['Warning: ''LoadFcn'' for RTI Data block failed: ' lasterr]); end, end,
  ModelCloseFcn = if exist('rtidc'), try,  rtidc('DataHostBlockClbModelClose', gcbh); catch, disp(['Warning: ''ModelCloseFcn'' for RTI Data block failed: ' lasterr]); end, end,
  NameChangeFcn = if exist('rtidc'), try,  rtidc('DataHostBlockClbNameChange', gcbh); catch, disp(['Warning: ''NameChangeFcn'' for RTI Data block failed: ' lasterr]); end, end,
  Ports = []
  PostSaveFcn = if exist('rtidc'), try,  rtidc('DataHostBlockClbPostSave', gcbh); catch, disp(['Warning: ''PostSaveFcn'' for RTI Data block failed: ' lasterr]); end, end,
  PreSaveFcn = if exist('rtidc'), try,  rtidc('DataHostBlockClbPreSave', gcbh); catch, disp(['Warning: ''PreSaveFcn'' for RTI Data block failed: ' lasterr]); end, end,
  RequestExecContextInheritance = off
  Tag = struct('RTIDataServer',struct('RTIDataServerVs','2','RTIModelDescription','struct(''main'',''main'',''sub'',''main'',''isMp'',0)'))
BLOCK [SubSystem] RTI Data/RTI Data Store
  Ports = []
  RequestExecContextInheritance = off
  Tag = struct('private',struct('version',struct('dsVer',uint32(2),'dsVerCreation',uint32(2),'RTI',struct('ver','7.4','type','RTI1005')),'access',struct('type','Model','isPerm',1,'created',['11-Mar-2019 14:33:50'],'modified',['18-Mar-2019 15:29:44'],'location','')),'public',struct('main',struct('data',[]),'sub',struct('name',{{'main'}},'data',{{struct('TH',struct('thTaskInfo',struct('taskType',{'TIMER','H...<+881ch>
BLOCK [SubSystem] RTI Data/RTI Data Store/RTI Data Store
  Ports = []
  RequestExecContextInheritance = off
BLOCK [SubSystem] RTI Data/RTI Data Store/RTI Data Store/RTI Data Store
  Ports = []
  RequestExecContextInheritance = off
BLOCK [SubSystem] RTI Data/RTI Data Store/RTI Data Store/RTI Data Store/RTI Data Store
  Ports = []
  RequestExecContextInheritance = off
BLOCK [SubSystem] Regulator P
  Ports = [2, 1]
  RequestExecContextInheritance = off
BLOCK [Constant] Regulator P/Constant
  Value = -0.3
BLOCK [Constant] Regulator P/Constant1
  Value = 0
BLOCK [DataStoreRead] Regulator P/Data Store Read10
  DataStoreName = czuj_baz_os_2
  Ports = [0, 1]
BLOCK [DataStoreRead] Regulator P/Data Store Read11
  DataStoreName = Bazowanie_on
  Ports = [0, 1]
BLOCK [DataStoreRead] Regulator P/Data Store Read12
  DataStoreName = Bazowanie_off
  Ports = [0, 1]
BLOCK [DataStoreRead] Regulator P/Data Store Read16
  DataStoreName = wpolczynnik_predkosci_roboczej
  Ports = [0, 1]
BLOCK [DataStoreWrite] Regulator P/Data Store Write1
  DataStoreName = os2_zad
  Ports = [1]
BLOCK [DataStoreWrite] Regulator P/Data Store Write8
  DataStoreName = reset_os_2
  Ports = [1]
BLOCK [Gain] Regulator P/Gain
  Gain = 0.5
  OutDataTypeStr = Inherit: Inherit via internal rule
  ParamDataTypeStr = Inherit: Inherit via internal rule
  SaturateOnIntegerOverflow = off
BLOCK [Gain] Regulator P/Gain1
  Gain = 0.1
  OutDataTypeStr = Inherit: Inherit via internal rule
  ParamDataTypeStr = Inherit: Inherit via internal rule
  SaturateOnIntegerOverflow = off
BLOCK [Logic] Regulator P/Logical Operator
  AllPortsSameDT = off
  Operator = OR
  Ports = [2, 1]
BLOCK [Product] Regulator P/Product
  InputSameDT = off
  OutDataTypeStr = Inherit: Inherit via internal rule
  Ports = [2, 1]
  RndMeth = Floor
  SaturateOnIntegerOverflow = off
BLOCK [RateLimiter] Regulator P/Rate Limiter
  FallingSlewLimit = -50
  RisingSlewLimit = 50
  SampleTimeMode = inherited
BLOCK [Reference] Regulator P/S-R Flip-Flop  REF=simulink_extras/Flip Flops/S-R
Flip-Flop
  Ports = [2, 2]
  SourceBlock = simulink_extras/Flip Flops/S-R
Flip-Flop
  SourceType = SRFlipFlop
  initial_condition = 0
BLOCK [Saturate] Regulator P/Saturation
  InputPortMap = u0
  LowerLimit = -3
  Ports = [1, 1]
  UpperLimit = 3
BLOCK [Sum] Regulator P/Sum
  IconShape = round
  InputSameDT = off
  Inputs = |+-
  OutDataTypeStr = Inherit: Inherit via internal rule
  Ports = [2, 1]
  SaturateOnIntegerOverflow = off
BLOCK [Switch] Regulator P/Switch
  Criteria = u2 > Threshold
  InputSameDT = off
  SaturateOnIntegerOverflow = off
BLOCK [Switch] Regulator P/Switch1
  Criteria = u2 > Threshold
  InputSameDT = off
  SaturateOnIntegerOverflow = off
BLOCK [Inport] Regulator P/pomiar 
  IconDisplay = Port number
  Port = 2
BLOCK [Outport] Regulator P/sterowanie
  IconDisplay = Port number
BLOCK [Inport] Regulator P/zadana
  IconDisplay = Port number
BLOCK [SubSystem] Regulator P1
  Ports = [2, 1]
  RequestExecContextInheritance = off
BLOCK [Constant] Regulator P1/Constant
  Value = -0.3
BLOCK [Constant] Regulator P1/Constant1
  Value = 0
BLOCK [DataStoreRead] Regulator P1/Data Store Read10
  DataStoreName = czuj_baz_os_1
  Ports = [0, 1]
BLOCK [DataStoreRead] Regulator P1/Data Store Read11
  DataStoreName = Bazowanie_on
  Ports = [0, 1]
BLOCK [DataStoreRead] Regulator P1/Data Store Read12
  DataStoreName = Bazowanie_off
  Ports = [0, 1]
BLOCK [DataStoreRead] Regulator P1/Data Store Read16
  DataStoreName = wpolczynnik_predkosci_roboczej
  Ports = [0, 1]
BLOCK [DataStoreWrite] Regulator P1/Data Store Write1
  DataStoreName = os1_zad
  Ports = [1]
BLOCK [DataStoreWrite] Regulator P1/Data Store Write8
  DataStoreName = reset_os_1
  Ports = [1]
BLOCK [Gain] Regulator P1/Gain
  Gain = 0.5
  OutDataTypeStr = Inherit: Inherit via internal rule
  ParamDataTypeStr = Inherit: Inherit via internal rule
  SaturateOnIntegerOverflow = off
BLOCK [Gain] Regulator P1/Gain1
  Gain = 0.1
  OutDataTypeStr = Inherit: Inherit via internal rule
  ParamDataTypeStr = Inherit: Inherit via internal rule
  SaturateOnIntegerOverflow = off
BLOCK [Logic] Regulator P1/Logical Operator
  AllPortsSameDT = off
  Operator = OR
  Ports = [2, 1]
BLOCK [Product] Regulator P1/Product
  InputSameDT = off
  OutDataTypeStr = Inherit: Inherit via internal rule
  Ports = [2, 1]
  RndMeth = Floor
  SaturateOnIntegerOverflow = off
BLOCK [RateLimiter] Regulator P1/Rate Limiter
  FallingSlewLimit = -50
  RisingSlewLimit = 50
  SampleTimeMode = inherited
BLOCK [Reference] Regulator P1/S-R Flip-Flop  REF=simulink_extras/Flip Flops/S-R
Flip-Flop
  Ports = [2, 2]
  SourceBlock = simulink_extras/Flip Flops/S-R
Flip-Flop
  SourceType = SRFlipFlop
  initial_condition = 0
BLOCK [Saturate] Regulator P1/Saturation
  InputPortMap = u0
  LowerLimit = -3
  Ports = [1, 1]
  UpperLimit = 3
BLOCK [Sum] Regulator P1/Sum
  IconShape = round
  InputSameDT = off
  Inputs = |+-
  OutDataTypeStr = Inherit: Inherit via internal rule
  Ports = [2, 1]
  SaturateOnIntegerOverflow = off
BLOCK [Switch] Regulator P1/Switch
  Criteria = u2 > Threshold
  InputSameDT = off
  SaturateOnIntegerOverflow = off
BLOCK [Switch] Regulator P1/Switch1
  Criteria = u2 > Threshold
  InputSameDT = off
  SaturateOnIntegerOverflow = off
BLOCK [Inport] Regulator P1/pomiar 
  IconDisplay = Port number
  Port = 2
BLOCK [Outport] Regulator P1/sterowanie
  IconDisplay = Port number
BLOCK [Inport] Regulator P1/zadana
  IconDisplay = Port number
BLOCK [SubSystem] Regulator P2
  Ports = [2, 1]
  RequestExecContextInheritance = off
BLOCK [DataStoreRead] Regulator P2/Data Store Read16
  DataStoreName = wpolczynnik_predkosci_roboczej
  Ports = [0, 1]
BLOCK [Gain] Regulator P2/Gain
  Gain = 0.5
  OutDataTypeStr = Inherit: Inherit via internal rule
  ParamDataTypeStr = Inherit: Inherit via internal rule
  SaturateOnIntegerOverflow = off
BLOCK [Gain] Regulator P2/Gain1
  Gain = 0.1
  OutDataTypeStr = Inherit: Inherit via internal rule
  ParamDataTypeStr = Inherit: Inherit via internal rule
  SaturateOnIntegerOverflow = off
BLOCK [Product] Regulator P2/Product
  InputSameDT = off
  OutDataTypeStr = Inherit: Inherit via internal rule
  Ports = [2, 1]
  RndMeth = Floor
  SaturateOnIntegerOverflow = off
BLOCK [RateLimiter] Regulator P2/Rate Limiter
  FallingSlewLimit = -50
  RisingSlewLimit = 50
  SampleTimeMode = inherited
BLOCK [Saturate] Regulator P2/Saturation
  InputPortMap = u0
  LowerLimit = -3
  Ports = [1, 1]
  UpperLimit = 3
BLOCK [Sum] Regulator P2/Sum
  IconShape = round
  InputSameDT = off
  Inputs = |+-
  OutDataTypeStr = Inherit: Inherit via internal rule
  Ports = [2, 1]
  SaturateOnIntegerOverflow = off
BLOCK [Inport] Regulator P2/pomiar 
  IconDisplay = Port number
  Port = 2
BLOCK [Outport] Regulator P2/sterowanie
  IconDisplay = Port number
BLOCK [Inport] Regulator P2/zadana
  IconDisplay = Port number
BLOCK [SubSystem] Regulator P3
  Ports = [2, 1]
  RequestExecContextInheritance = off
BLOCK [Constant] Regulator P3/Constant
  Value = -0.3
BLOCK [Constant] Regulator P3/Constant1
  Value = 0
BLOCK [DataStoreRead] Regulator P3/Data Store Read10
  DataStoreName = czuj_baz_os_3
  Ports = [0, 1]
BLOCK [DataStoreRead] Regulator P3/Data Store Read11
  DataStoreName = Bazowanie_on
  Ports = [0, 1]
BLOCK [DataStoreRead] Regulator P3/Data Store Read12
  DataStoreName = Bazowanie_off
  Ports = [0, 1]
BLOCK [DataStoreRead] Regulator P3/Data Store Read16
  DataStoreName = wpolczynnik_predkosci_roboczej
  Ports = [0, 1]
BLOCK [DataStoreWrite] Regulator P3/Data Store Write1
  DataStoreName = os3_zad
  Ports = [1]
BLOCK [DataStoreWrite] Regulator P3/Data Store Write8
  DataStoreName = reset_os_3
  Ports = [1]
BLOCK [Gain] Regulator P3/Gain2
  Gain = 0.5
  OutDataTypeStr = Inherit: Inherit via internal rule
  ParamDataTypeStr = Inherit: Inherit via internal rule
  SaturateOnIntegerOverflow = off
BLOCK [Gain] Regulator P3/Gain3
  Gain = 0.1
  OutDataTypeStr = Inherit: Inherit via internal rule
  ParamDataTypeStr = Inherit: Inherit via internal rule
  SaturateOnIntegerOverflow = off
BLOCK [Logic] Regulator P3/Logical Operator
  AllPortsSameDT = off
  Operator = OR
  Ports = [2, 1]
BLOCK [Product] Regulator P3/Product
  InputSameDT = off
  OutDataTypeStr = Inherit: Inherit via internal rule
  Ports = [2, 1]
  RndMeth = Floor
  SaturateOnIntegerOverflow = off
BLOCK [RateLimiter] Regulator P3/Rate Limiter1
  FallingSlewLimit = -50
  RisingSlewLimit = 50
  SampleTimeMode = inherited
BLOCK [Reference] Regulator P3/S-R Flip-Flop  REF=simulink_extras/Flip Flops/S-R
Flip-Flop
  Ports = [2, 2]
  SourceBlock = simulink_extras/Flip Flops/S-R
Flip-Flop
  SourceType = SRFlipFlop
  initial_condition = 0
BLOCK [Saturate] Regulator P3/Saturation1
  InputPortMap = u0
  LowerLimit = -3
  Ports = [1, 1]
  UpperLimit = 3
BLOCK [Sum] Regulator P3/Sum1
  IconShape = round
  InputSameDT = off
  Inputs = |+-
  OutDataTypeStr = Inherit: Inherit via internal rule
  Ports = [2, 1]
  SaturateOnIntegerOverflow = off
BLOCK [Switch] Regulator P3/Switch
  Criteria = u2 > Threshold
  InputSameDT = off
  SaturateOnIntegerOverflow = off
BLOCK [Switch] Regulator P3/Switch1
  Criteria = u2 > Threshold
  InputSameDT = off
  SaturateOnIntegerOverflow = off
BLOCK [Inport] Regulator P3/pomiar 2
  IconDisplay = Port number
  Port = 2
BLOCK [Outport] Regulator P3/sterowanie
  IconDisplay = Port number
BLOCK [Inport] Regulator P3/zadana
  IconDisplay = Port number
BLOCK [SubSystem] Regulator P4
  Ports = [2, 1]
  RequestExecContextInheritance = off
BLOCK [DataStoreRead] Regulator P4/Data Store Read16
  DataStoreName = wpolczynnik_predkosci_roboczej
  Ports = [0, 1]
BLOCK [Gain] Regulator P4/Gain
  Gain = 0.5
  OutDataTypeStr = Inherit: Inherit via internal rule
  ParamDataTypeStr = Inherit: Inherit via internal rule
  SaturateOnIntegerOverflow = off
BLOCK [Gain] Regulator P4/Gain1
  Gain = 0.1
  OutDataTypeStr = Inherit: Inherit via internal rule
  ParamDataTypeStr = Inherit: Inherit via internal rule
  SaturateOnIntegerOverflow = off
BLOCK [Product] Regulator P4/Product
  InputSameDT = off
  OutDataTypeStr = Inherit: Inherit via internal rule
  Ports = [2, 1]
  RndMeth = Floor
  SaturateOnIntegerOverflow = off
BLOCK [RateLimiter] Regulator P4/Rate Limiter
  FallingSlewLimit = -50
  RisingSlewLimit = 50
  SampleTimeMode = inherited
BLOCK [Saturate] Regulator P4/Saturation
  InputPortMap = u0
  LowerLimit = -3
  Ports = [1, 1]
  UpperLimit = 3
BLOCK [Sum] Regulator P4/Sum
  IconShape = round
  InputSameDT = off
  Inputs = |+-
  OutDataTypeStr = Inherit: Inherit via internal rule
  Ports = [2, 1]
  SaturateOnIntegerOverflow = off
BLOCK [Inport] Regulator P4/pomiar 
  IconDisplay = Port number
  Port = 2
BLOCK [Outport] Regulator P4/sterowanie
  IconDisplay = Port number
BLOCK [Inport] Regulator P4/zadana
  IconDisplay = Port number
BLOCK [Saturate] Saturation
  InputPortMap = u0
  LowerLimit = 5
  Ports = [1, 1]
  UpperLimit = 100
BLOCK [Terminator] Terminator
BLOCK [Terminator] Terminator1
BLOCK [DataStoreMemory] os1
  DataStoreName = os1_zad
  ReadBeforeWriteMsg = warning
  WriteAfterReadMsg = warning
  WriteAfterWriteMsg = warning
BLOCK [DataStoreMemory] os1_panel 
  DataStoreName = os1_panel
  ReadBeforeWriteMsg = warning
  WriteAfterReadMsg = warning
  WriteAfterWriteMsg = warning
BLOCK [Constant] os4_reset
  OutDataTypeStr = double
BLOCK [Constant] os5_reset 
  OutDataTypeStr = double
LINE DS2201ADC_B1:1 -> Demux:1
LINE DS2201ADC_B1:2 -> Demux1:1
LINE DS2201ADC_B1:3 -> Position 5:1
LINE DS2201ADC_B1:4 -> Terminator:1
LINE DS2201ADC_B1:5 -> Terminator1:1
LINE DS2201IN_B3:1 -> Demux2:1
LINE Data Store Read11:1 -> Position 3:2
LINE Data Store Read13:1 -> Position 2:2
LINE Data Store Read14:1 -> Position 1:2
LINE Data Store Read15:1 -> Saturation:1
LINE Data Store Read1:1 -> Regulator P:1
LINE Data Store Read2:1 -> Regulator P3:1
LINE Data Store Read3:1 -> Regulator P2:1
LINE Data Store Read4:1 -> Regulator P4:1
LINE Data Store Read5:1 -> Moduł sprawdzający czy wpisana pozycja dla ruchu, może być wartością zadaną dla regulatorów P, praz podana na elementy wykonawcze2:1
LINE Data Store Read6:1 -> Moduł sprawdzający czy wpisana pozycja dla ruchu, może być wartością zadaną dla regulatorów P, praz podana na elementy wykonawcze2:2
LINE Data Store Read7:1 -> Moduł sprawdzający czy wpisana pozycja dla ruchu, może być wartością zadaną dla regulatorów P, praz podana na elementy wykonawcze2:3
LINE Data Store Read8:1 -> Moduł sprawdzający czy wpisana pozycja dla ruchu, może być wartością zadaną dla regulatorów P, praz podana na elementy wykonawcze2:4
LINE Data Store Read9:1 -> Moduł sprawdzający czy wpisana pozycja dla ruchu, może być wartością zadaną dla regulatorów P, praz podana na elementy wykonawcze2:5
LINE Data Store Read:1 -> Regulator P1:1
LINE Demux1:1 -> Position 3:1
LINE Demux1:2 -> Position 4:1
LINE Demux2:1 -> Data Store Write5:1
LINE Demux2:2 -> Data Store Write6:1
LINE Demux2:3 -> Data Store Write7:1
LINE Demux:1 -> Position 1:1
LINE Demux:2 -> Position 2:1
LINE From1:1 -> Regulator P:2
LINE From2:1 -> Regulator P3:2
LINE From3:1 -> Regulator P2:2
LINE From4:1 -> Regulator P4:2
LINE From:1 -> Regulator P1:2
LINE Gain:1 -> Data Store Write8:1
LINE Ground1:1 -> DS2201DAC_B1:7
LINE Ground2:1 -> DS2201DAC_B1:6
LINE Ground:1 -> DS2201DAC_B1:8
LINE Moduł sprawdzający czy wpisana pozycja dla ruchu, może być wartością zadaną dla regulatorów P, praz podana na elementy wykonawcze2/Abs1:1 -> Moduł sprawdzający czy wpisana pozycja dla ruchu, może być wartością zadaną dla regulatorów P, praz podana na elementy wykonawcze2/Sum1:1
LINE Moduł sprawdzający czy wpisana pozycja dla ruchu, może być wartością zadaną dla regulatorów P, praz podana na elementy wykonawcze2/Abs2:1 -> Moduł sprawdzający czy wpisana pozycja dla ruchu, może być wartością zadaną dla regulatorów P, praz podana na elementy wykonawcze2/Sum9:1
LINE Moduł sprawdzający czy wpisana pozycja dla ruchu, może być wartością zadaną dla regulatorów P, praz podana na elementy wykonawcze2/Abs:1 -> Moduł sprawdzający czy wpisana pozycja dla ruchu, może być wartością zadaną dla regulatorów P, praz podana na elementy wykonawcze2/Sum:1
LINE Moduł sprawdzający czy wpisana pozycja dla ruchu, może być wartością zadaną dla regulatorów P, praz podana na elementy wykonawcze2/Constant10:1 -> Moduł sprawdzający czy wpisana pozycja dla ruchu, może być wartością zadaną dla regulatorów P, praz podana na elementy wykonawcze2/Switch3:3
LINE Moduł sprawdzający czy wpisana pozycja dla ruchu, może być wartością zadaną dla regulatorów P, praz podana na elementy wykonawcze2/Constant11:1 -> Moduł sprawdzający czy wpisana pozycja dla ruchu, może być wartością zadaną dla regulatorów P, praz podana na elementy wykonawcze2/Switch5:3
LINE Moduł sprawdzający czy wpisana pozycja dla ruchu, może być wartością zadaną dla regulatorów P, praz podana na elementy wykonawcze2/Constant12:1 -> Moduł sprawdzający czy wpisana pozycja dla ruchu, może być wartością zadaną dla regulatorów P, praz podana na elementy wykonawcze2/Sum4:2
LINE Moduł sprawdzający czy wpisana pozycja dla ruchu, może być wartością zadaną dla regulatorów P, praz podana na elementy wykonawcze2/Constant13:1 -> Moduł sprawdzający czy wpisana pozycja dla ruchu, może być wartością zadaną dla regulatorów P, praz podana na elementy wykonawcze2/Switch4:1
LINE Moduł sprawdzający czy wpisana pozycja dla ruchu, może być wartością zadaną dla regulatorów P, praz podana na elementy wykonawcze2/Constant14:1 -> Moduł sprawdzający czy wpisana pozycja dla ruchu, może być wartością zadaną dla regulatorów P, praz podana na elementy wykonawcze2/Switch4:3
LINE Moduł sprawdzający czy wpisana pozycja dla ruchu, może być wartością zadaną dla regulatorów P, praz podana na elementy wykonawcze2/Constant14:1 -> Moduł sprawdzający czy wpisana pozycja dla ruchu, może być wartością zadaną dla regulatorów P, praz podana na elementy wykonawcze2/Switch5:1
LINE Moduł sprawdzający czy wpisana pozycja dla ruchu, może być wartością zadaną dla regulatorów P, praz podana na elementy wykonawcze2/Constant15:1 -> Moduł sprawdzający czy wpisana pozycja dla ruchu, może być wartością zadaną dla regulatorów P, praz podana na elementy wykonawcze2/Sum5:2
LINE Moduł sprawdzający czy wpisana pozycja dla ruchu, może być wartością zadaną dla regulatorów P, praz podana na elementy wykonawcze2/Constant16:1 -> Moduł sprawdzający czy wpisana pozycja dla ruchu, może być wartością zadaną dla regulatorów P, praz podana na elementy wykonawcze2/Switch7:3
LINE Moduł sprawdzający czy wpisana pozycja dla ruchu, może być wartością zadaną dla regulatorów P, praz podana na elementy wykonawcze2/Constant17:1 -> Moduł sprawdzający czy wpisana pozycja dla ruchu, może być wartością zadaną dla regulatorów P, praz podana na elementy wykonawcze2/Sum6:2
LINE Moduł sprawdzający czy wpisana pozycja dla ruchu, może być wartością zadaną dla regulatorów P, praz podana na elementy wykonawcze2/Constant18:1 -> Moduł sprawdzający czy wpisana pozycja dla ruchu, może być wartością zadaną dla regulatorów P, praz podana na elementy wykonawcze2/Switch6:1
LINE Moduł sprawdzający czy wpisana pozycja dla ruchu, może być wartością zadaną dla regulatorów P, praz podana na elementy wykonawcze2/Constant19:1 -> Moduł sprawdzający czy wpisana pozycja dla ruchu, może być wartością zadaną dla regulatorów P, praz podana na elementy wykonawcze2/Switch6:3
LINE Moduł sprawdzający czy wpisana pozycja dla ruchu, może być wartością zadaną dla regulatorów P, praz podana na elementy wykonawcze2/Constant19:1 -> Moduł sprawdzający czy wpisana pozycja dla ruchu, może być wartością zadaną dla regulatorów P, praz podana na elementy wykonawcze2/Switch7:1
LINE Moduł sprawdzający czy wpisana pozycja dla ruchu, może być wartością zadaną dla regulatorów P, praz podana na elementy wykonawcze2/Constant1:1 -> Moduł sprawdzający czy wpisana pozycja dla ruchu, może być wartością zadaną dla regulatorów P, praz podana na elementy wykonawcze2/Switch:3
LINE Moduł sprawdzający czy wpisana pozycja dla ruchu, może być wartością zadaną dla regulatorów P, praz podana na elementy wykonawcze2/Constant20:1 -> Moduł sprawdzający czy wpisana pozycja dla ruchu, może być wartością zadaną dla regulatorów P, praz podana na elementy wykonawcze2/Sum7:2
LINE Moduł sprawdzający czy wpisana pozycja dla ruchu, może być wartością zadaną dla regulatorów P, praz podana na elementy wykonawcze2/Constant21:1 -> Moduł sprawdzający czy wpisana pozycja dla ruchu, może być wartością zadaną dla regulatorów P, praz podana na elementy wykonawcze2/Sum9:2
LINE Moduł sprawdzający czy wpisana pozycja dla ruchu, może być wartością zadaną dla regulatorów P, praz podana na elementy wykonawcze2/Constant22:1 -> Moduł sprawdzający czy wpisana pozycja dla ruchu, może być wartością zadaną dla regulatorów P, praz podana na elementy wykonawcze2/Switch8:1
LINE Moduł sprawdzający czy wpisana pozycja dla ruchu, może być wartością zadaną dla regulatorów P, praz podana na elementy wykonawcze2/Constant23:1 -> Moduł sprawdzający czy wpisana pozycja dla ruchu, może być wartością zadaną dla regulatorów P, praz podana na elementy wykonawcze2/Switch8:3
LINE Moduł sprawdzający czy wpisana pozycja dla ruchu, może być wartością zadaną dla regulatorów P, praz podana na elementy wykonawcze2/Constant2:1 -> Moduł sprawdzający czy wpisana pozycja dla ruchu, może być wartością zadaną dla regulatorów P, praz podana na elementy wykonawcze2/Switch:1
LINE Moduł sprawdzający czy wpisana pozycja dla ruchu, może być wartością zadaną dla regulatorów P, praz podana na elementy wykonawcze2/Constant3:1 -> Moduł sprawdzający czy wpisana pozycja dla ruchu, może być wartością zadaną dla regulatorów P, praz podana na elementy wykonawcze2/Sum1:2
LINE Moduł sprawdzający czy wpisana pozycja dla ruchu, może być wartością zadaną dla regulatorów P, praz podana na elementy wykonawcze2/Constant4:1 -> Moduł sprawdzający czy wpisana pozycja dla ruchu, może być wartością zadaną dla regulatorów P, praz podana na elementy wykonawcze2/Switch1:3
LINE Moduł sprawdzający czy wpisana pozycja dla ruchu, może być wartością zadaną dla regulatorów P, praz podana na elementy wykonawcze2/Constant5:1 -> Moduł sprawdzający czy wpisana pozycja dla ruchu, może być wartością zadaną dla regulatorów P, praz podana na elementy wykonawcze2/Switch1:1
LINE Moduł sprawdzający czy wpisana pozycja dla ruchu, może być wartością zadaną dla regulatorów P, praz podana na elementy wykonawcze2/Constant6:1 -> Moduł sprawdzający czy wpisana pozycja dla ruchu, może być wartością zadaną dla regulatorów P, praz podana na elementy wykonawcze2/Sum2:2
LINE Moduł sprawdzający czy wpisana pozycja dla ruchu, może być wartością zadaną dla regulatorów P, praz podana na elementy wykonawcze2/Constant7:1 -> Moduł sprawdzający czy wpisana pozycja dla ruchu, może być wartością zadaną dla regulatorów P, praz podana na elementy wykonawcze2/Switch2:1
LINE Moduł sprawdzający czy wpisana pozycja dla ruchu, może być wartością zadaną dla regulatorów P, praz podana na elementy wykonawcze2/Constant8:1 -> Moduł sprawdzający czy wpisana pozycja dla ruchu, może być wartością zadaną dla regulatorów P, praz podana na elementy wykonawcze2/Switch2:3
LINE Moduł sprawdzający czy wpisana pozycja dla ruchu, może być wartością zadaną dla regulatorów P, praz podana na elementy wykonawcze2/Constant8:1 -> Moduł sprawdzający czy wpisana pozycja dla ruchu, może być wartością zadaną dla regulatorów P, praz podana na elementy wykonawcze2/Switch3:1
LINE Moduł sprawdzający czy wpisana pozycja dla ruchu, może być wartością zadaną dla regulatorów P, praz podana na elementy wykonawcze2/Constant9:1 -> Moduł sprawdzający czy wpisana pozycja dla ruchu, może być wartością zadaną dla regulatorów P, praz podana na elementy wykonawcze2/Sum3:2
LINE Moduł sprawdzający czy wpisana pozycja dla ruchu, może być wartością zadaną dla regulatorów P, praz podana na elementy wykonawcze2/Constant:1 -> Moduł sprawdzający czy wpisana pozycja dla ruchu, może być wartością zadaną dla regulatorów P, praz podana na elementy wykonawcze2/Sum:2
LINE Moduł sprawdzający czy wpisana pozycja dla ruchu, może być wartością zadaną dla regulatorów P, praz podana na elementy wykonawcze2/Data Store Read17:1 -> Moduł sprawdzający czy wpisana pozycja dla ruchu, może być wartością zadaną dla regulatorów P, praz podana na elementy wykonawcze2/Switch9:3
LINE Moduł sprawdzający czy wpisana pozycja dla ruchu, może być wartością zadaną dla regulatorów P, praz podana na elementy wykonawcze2/Data Store Read18:1 -> Moduł sprawdzający czy wpisana pozycja dla ruchu, może być wartością zadaną dla regulatorów P, praz podana na elementy wykonawcze2/Switch10:3
LINE Moduł sprawdzający czy wpisana pozycja dla ruchu, może być wartością zadaną dla regulatorów P, praz podana na elementy wykonawcze2/Data Store Read19:1 -> Moduł sprawdzający czy wpisana pozycja dla ruchu, może być wartością zadaną dla regulatorów P, praz podana na elementy wykonawcze2/Switch11:3
LINE Moduł sprawdzający czy wpisana pozycja dla ruchu, może być wartością zadaną dla regulatorów P, praz podana na elementy wykonawcze2/Data Store Read20:1 -> Moduł sprawdzający czy wpisana pozycja dla ruchu, może być wartością zadaną dla regulatorów P, praz podana na elementy wykonawcze2/Switch12:3
LINE Moduł sprawdzający czy wpisana pozycja dla ruchu, może być wartością zadaną dla regulatorów P, praz podana na elementy wykonawcze2/Data Store Read21:1 -> Moduł sprawdzający czy wpisana pozycja dla ruchu, może być wartością zadaną dla regulatorów P, praz podana na elementy wykonawcze2/Switch13:3
LINE Moduł sprawdzający czy wpisana pozycja dla ruchu, może być wartością zadaną dla regulatorów P, praz podana na elementy wykonawcze2/From1:1 -> Moduł sprawdzający czy wpisana pozycja dla ruchu, może być wartością zadaną dla regulatorów P, praz podana na elementy wykonawcze2/Sum8:2
LINE Moduł sprawdzający czy wpisana pozycja dla ruchu, może być wartością zadaną dla regulatorów P, praz podana na elementy wykonawcze2/From2:1 -> Moduł sprawdzający czy wpisana pozycja dla ruchu, może być wartością zadaną dla regulatorów P, praz podana na elementy wykonawcze2/Switch13:1
LINE Moduł sprawdzający czy wpisana pozycja dla ruchu, może być wartością zadaną dla regulatorów P, praz podana na elementy wykonawcze2/From3:1 -> Moduł sprawdzający czy wpisana pozycja dla ruchu, może być wartością zadaną dla regulatorów P, praz podana na elementy wykonawcze2/Switch10:1
LINE Moduł sprawdzający czy wpisana pozycja dla ruchu, może być wartością zadaną dla regulatorów P, praz podana na elementy wykonawcze2/From4:1 -> Moduł sprawdzający czy wpisana pozycja dla ruchu, może być wartością zadaną dla regulatorów P, praz podana na elementy wykonawcze2/Switch9:1
LINE Moduł sprawdzający czy wpisana pozycja dla ruchu, może być wartością zadaną dla regulatorów P, praz podana na elementy wykonawcze2/From5:1 -> Moduł sprawdzający czy wpisana pozycja dla ruchu, może być wartością zadaną dla regulatorów P, praz podana na elementy wykonawcze2/Switch12:1
LINE Moduł sprawdzający czy wpisana pozycja dla ruchu, może być wartością zadaną dla regulatorów P, praz podana na elementy wykonawcze2/From6:1 -> Moduł sprawdzający czy wpisana pozycja dla ruchu, może być wartością zadaną dla regulatorów P, praz podana na elementy wykonawcze2/Switch11:1
LINE Moduł sprawdzający czy wpisana pozycja dla ruchu, może być wartością zadaną dla regulatorów P, praz podana na elementy wykonawcze2/From:1 -> Moduł sprawdzający czy wpisana pozycja dla ruchu, może być wartością zadaną dla regulatorów P, praz podana na elementy wykonawcze2/Sum8:1
LINE Moduł sprawdzający czy wpisana pozycja dla ruchu, może być wartością zadaną dla regulatorów P, praz podana na elementy wykonawcze2/Logical Operator1:1 -> Moduł sprawdzający czy wpisana pozycja dla ruchu, może być wartością zadaną dla regulatorów P, praz podana na elementy wykonawcze2/Logical Operator3:5
LINE Moduł sprawdzający czy wpisana pozycja dla ruchu, może być wartością zadaną dla regulatorów P, praz podana na elementy wykonawcze2/Logical Operator2:1 -> Moduł sprawdzający czy wpisana pozycja dla ruchu, może być wartością zadaną dla regulatorów P, praz podana na elementy wykonawcze2/Logical Operator3:4
LINE Moduł sprawdzający czy wpisana pozycja dla ruchu, może być wartością zadaną dla regulatorów P, praz podana na elementy wykonawcze2/Logical Operator3:1 -> Moduł sprawdzający czy wpisana pozycja dla ruchu, może być wartością zadaną dla regulatorów P, praz podana na elementy wykonawcze2/Switch10:2
LINE Moduł sprawdzający czy wpisana pozycja dla ruchu, może być wartością zadaną dla regulatorów P, praz podana na elementy wykonawcze2/Logical Operator3:1 -> Moduł sprawdzający czy wpisana pozycja dla ruchu, może być wartością zadaną dla regulatorów P, praz podana na elementy wykonawcze2/Switch11:2
LINE Moduł sprawdzający czy wpisana pozycja dla ruchu, może być wartością zadaną dla regulatorów P, praz podana na elementy wykonawcze2/Logical Operator3:1 -> Moduł sprawdzający czy wpisana pozycja dla ruchu, może być wartością zadaną dla regulatorów P, praz podana na elementy wykonawcze2/Switch12:2
LINE Moduł sprawdzający czy wpisana pozycja dla ruchu, może być wartością zadaną dla regulatorów P, praz podana na elementy wykonawcze2/Logical Operator3:1 -> Moduł sprawdzający czy wpisana pozycja dla ruchu, może być wartością zadaną dla regulatorów P, praz podana na elementy wykonawcze2/Switch13:2
LINE Moduł sprawdzający czy wpisana pozycja dla ruchu, może być wartością zadaną dla regulatorów P, praz podana na elementy wykonawcze2/Logical Operator3:1 -> Moduł sprawdzający czy wpisana pozycja dla ruchu, może być wartością zadaną dla regulatorów P, praz podana na elementy wykonawcze2/Switch9:2
LINE Moduł sprawdzający czy wpisana pozycja dla ruchu, może być wartością zadaną dla regulatorów P, praz podana na elementy wykonawcze2/Logical Operator:1 -> Moduł sprawdzający czy wpisana pozycja dla ruchu, może być wartością zadaną dla regulatorów P, praz podana na elementy wykonawcze2/Logical Operator3:3
LINE Moduł sprawdzający czy wpisana pozycja dla ruchu, może być wartością zadaną dla regulatorów P, praz podana na elementy wykonawcze2/Sum1:1 -> Moduł sprawdzający czy wpisana pozycja dla ruchu, może być wartością zadaną dla regulatorów P, praz podana na elementy wykonawcze2/Switch1:2
LINE Moduł sprawdzający czy wpisana pozycja dla ruchu, może być wartością zadaną dla regulatorów P, praz podana na elementy wykonawcze2/Sum2:1 -> Moduł sprawdzający czy wpisana pozycja dla ruchu, może być wartością zadaną dla regulatorów P, praz podana na elementy wykonawcze2/Switch2:2
LINE Moduł sprawdzający czy wpisana pozycja dla ruchu, może być wartością zadaną dla regulatorów P, praz podana na elementy wykonawcze2/Sum3:1 -> Moduł sprawdzający czy wpisana pozycja dla ruchu, może być wartością zadaną dla regulatorów P, praz podana na elementy wykonawcze2/Switch3:2
LINE Moduł sprawdzający czy wpisana pozycja dla ruchu, może być wartością zadaną dla regulatorów P, praz podana na elementy wykonawcze2/Sum4:1 -> Moduł sprawdzający czy wpisana pozycja dla ruchu, może być wartością zadaną dla regulatorów P, praz podana na elementy wykonawcze2/Switch4:2
LINE Moduł sprawdzający czy wpisana pozycja dla ruchu, może być wartością zadaną dla regulatorów P, praz podana na elementy wykonawcze2/Sum5:1 -> Moduł sprawdzający czy wpisana pozycja dla ruchu, może być wartością zadaną dla regulatorów P, praz podana na elementy wykonawcze2/Switch5:2
LINE Moduł sprawdzający czy wpisana pozycja dla ruchu, może być wartością zadaną dla regulatorów P, praz podana na elementy wykonawcze2/Sum6:1 -> Moduł sprawdzający czy wpisana pozycja dla ruchu, może być wartością zadaną dla regulatorów P, praz podana na elementy wykonawcze2/Switch6:2
LINE Moduł sprawdzający czy wpisana pozycja dla ruchu, może być wartością zadaną dla regulatorów P, praz podana na elementy wykonawcze2/Sum7:1 -> Moduł sprawdzający czy wpisana pozycja dla ruchu, może być wartością zadaną dla regulatorów P, praz podana na elementy wykonawcze2/Switch7:2
LINE Moduł sprawdzający czy wpisana pozycja dla ruchu, może być wartością zadaną dla regulatorów P, praz podana na elementy wykonawcze2/Sum8:1 -> Moduł sprawdzający czy wpisana pozycja dla ruchu, może być wartością zadaną dla regulatorów P, praz podana na elementy wykonawcze2/Abs2:1
LINE Moduł sprawdzający czy wpisana pozycja dla ruchu, może być wartością zadaną dla regulatorów P, praz podana na elementy wykonawcze2/Sum9:1 -> Moduł sprawdzający czy wpisana pozycja dla ruchu, może być wartością zadaną dla regulatorów P, praz podana na elementy wykonawcze2/Switch8:2
LINE Moduł sprawdzający czy wpisana pozycja dla ruchu, może być wartością zadaną dla regulatorów P, praz podana na elementy wykonawcze2/Sum:1 -> Moduł sprawdzający czy wpisana pozycja dla ruchu, może być wartością zadaną dla regulatorów P, praz podana na elementy wykonawcze2/Switch:2
LINE Moduł sprawdzający czy wpisana pozycja dla ruchu, może być wartością zadaną dla regulatorów P, praz podana na elementy wykonawcze2/Switch10:1 -> Moduł sprawdzający czy wpisana pozycja dla ruchu, może być wartością zadaną dla regulatorów P, praz podana na elementy wykonawcze2/os_2:1
LINE Moduł sprawdzający czy wpisana pozycja dla ruchu, może być wartością zadaną dla regulatorów P, praz podana na elementy wykonawcze2/Switch11:1 -> Moduł sprawdzający czy wpisana pozycja dla ruchu, może być wartością zadaną dla regulatorów P, praz podana na elementy wykonawcze2/os_3:1
LINE Moduł sprawdzający czy wpisana pozycja dla ruchu, może być wartością zadaną dla regulatorów P, praz podana na elementy wykonawcze2/Switch12:1 -> Moduł sprawdzający czy wpisana pozycja dla ruchu, może być wartością zadaną dla regulatorów P, praz podana na elementy wykonawcze2/os_4:1
LINE Moduł sprawdzający czy wpisana pozycja dla ruchu, może być wartością zadaną dla regulatorów P, praz podana na elementy wykonawcze2/Switch13:1 -> Moduł sprawdzający czy wpisana pozycja dla ruchu, może być wartością zadaną dla regulatorów P, praz podana na elementy wykonawcze2/os_5:1
LINE Moduł sprawdzający czy wpisana pozycja dla ruchu, może być wartością zadaną dla regulatorów P, praz podana na elementy wykonawcze2/Switch1:1 -> Moduł sprawdzający czy wpisana pozycja dla ruchu, może być wartością zadaną dla regulatorów P, praz podana na elementy wykonawcze2/Logical Operator3:2
LINE Moduł sprawdzający czy wpisana pozycja dla ruchu, może być wartością zadaną dla regulatorów P, praz podana na elementy wykonawcze2/Switch2:1 -> Moduł sprawdzający czy wpisana pozycja dla ruchu, może być wartością zadaną dla regulatorów P, praz podana na elementy wykonawcze2/Logical Operator:1
LINE Moduł sprawdzający czy wpisana pozycja dla ruchu, może być wartością zadaną dla regulatorów P, praz podana na elementy wykonawcze2/Switch3:1 -> Moduł sprawdzający czy wpisana pozycja dla ruchu, może być wartością zadaną dla regulatorów P, praz podana na elementy wykonawcze2/Logical Operator:2
LINE Moduł sprawdzający czy wpisana pozycja dla ruchu, może być wartością zadaną dla regulatorów P, praz podana na elementy wykonawcze2/Switch4:1 -> Moduł sprawdzający czy wpisana pozycja dla ruchu, może być wartością zadaną dla regulatorów P, praz podana na elementy wykonawcze2/Logical Operator1:1
LINE Moduł sprawdzający czy wpisana pozycja dla ruchu, może być wartością zadaną dla regulatorów P, praz podana na elementy wykonawcze2/Switch5:1 -> Moduł sprawdzający czy wpisana pozycja dla ruchu, może być wartością zadaną dla regulatorów P, praz podana na elementy wykonawcze2/Logical Operator1:2
LINE Moduł sprawdzający czy wpisana pozycja dla ruchu, może być wartością zadaną dla regulatorów P, praz podana na elementy wykonawcze2/Switch6:1 -> Moduł sprawdzający czy wpisana pozycja dla ruchu, może być wartością zadaną dla regulatorów P, praz podana na elementy wykonawcze2/Logical Operator2:1
LINE Moduł sprawdzający czy wpisana pozycja dla ruchu, może być wartością zadaną dla regulatorów P, praz podana na elementy wykonawcze2/Switch7:1 -> Moduł sprawdzający czy wpisana pozycja dla ruchu, może być wartością zadaną dla regulatorów P, praz podana na elementy wykonawcze2/Logical Operator2:2
LINE Moduł sprawdzający czy wpisana pozycja dla ruchu, może być wartością zadaną dla regulatorów P, praz podana na elementy wykonawcze2/Switch8:1 -> Moduł sprawdzający czy wpisana pozycja dla ruchu, może być wartością zadaną dla regulatorów P, praz podana na elementy wykonawcze2/Logical Operator3:6
LINE Moduł sprawdzający czy wpisana pozycja dla ruchu, może być wartością zadaną dla regulatorów P, praz podana na elementy wykonawcze2/Switch9:1 -> Moduł sprawdzający czy wpisana pozycja dla ruchu, może być wartością zadaną dla regulatorów P, praz podana na elementy wykonawcze2/os_1:1
LINE Moduł sprawdzający czy wpisana pozycja dla ruchu, może być wartością zadaną dla regulatorów P, praz podana na elementy wykonawcze2/Switch:1 -> Moduł sprawdzający czy wpisana pozycja dla ruchu, może być wartością zadaną dla regulatorów P, praz podana na elementy wykonawcze2/Logical Operator3:1
LINE Moduł sprawdzający czy wpisana pozycja dla ruchu, może być wartością zadaną dla regulatorów P, praz podana na elementy wykonawcze2/os1_:1 -> Moduł sprawdzający czy wpisana pozycja dla ruchu, może być wartością zadaną dla regulatorów P, praz podana na elementy wykonawcze2/Abs:1
LINE Moduł sprawdzający czy wpisana pozycja dla ruchu, może być wartością zadaną dla regulatorów P, praz podana na elementy wykonawcze2/os1_:1 -> Moduł sprawdzający czy wpisana pozycja dla ruchu, może być wartością zadaną dla regulatorów P, praz podana na elementy wykonawcze2/Goto:1
LINE Moduł sprawdzający czy wpisana pozycja dla ruchu, może być wartością zadaną dla regulatorów P, praz podana na elementy wykonawcze2/os2:1 -> Moduł sprawdzający czy wpisana pozycja dla ruchu, może być wartością zadaną dla regulatorów P, praz podana na elementy wykonawcze2/Abs1:1
LINE Moduł sprawdzający czy wpisana pozycja dla ruchu, może być wartością zadaną dla regulatorów P, praz podana na elementy wykonawcze2/os2:1 -> Moduł sprawdzający czy wpisana pozycja dla ruchu, może być wartością zadaną dla regulatorów P, praz podana na elementy wykonawcze2/Goto1:1
LINE Moduł sprawdzający czy wpisana pozycja dla ruchu, może być wartością zadaną dla regulatorów P, praz podana na elementy wykonawcze2/os3:1 -> Moduł sprawdzający czy wpisana pozycja dla ruchu, może być wartością zadaną dla regulatorów P, praz podana na elementy wykonawcze2/Goto3:1
LINE Moduł sprawdzający czy wpisana pozycja dla ruchu, może być wartością zadaną dla regulatorów P, praz podana na elementy wykonawcze2/os3:1 -> Moduł sprawdzający czy wpisana pozycja dla ruchu, może być wartością zadaną dla regulatorów P, praz podana na elementy wykonawcze2/Sum2:1
LINE Moduł sprawdzający czy wpisana pozycja dla ruchu, może być wartością zadaną dla regulatorów P, praz podana na elementy wykonawcze2/os3:1 -> Moduł sprawdzający czy wpisana pozycja dla ruchu, może być wartością zadaną dla regulatorów P, praz podana na elementy wykonawcze2/Sum3:1
LINE Moduł sprawdzający czy wpisana pozycja dla ruchu, może być wartością zadaną dla regulatorów P, praz podana na elementy wykonawcze2/os4:1 -> Moduł sprawdzający czy wpisana pozycja dla ruchu, może być wartością zadaną dla regulatorów P, praz podana na elementy wykonawcze2/Goto4:1
LINE Moduł sprawdzający czy wpisana pozycja dla ruchu, może być wartością zadaną dla regulatorów P, praz podana na elementy wykonawcze2/os4:1 -> Moduł sprawdzający czy wpisana pozycja dla ruchu, może być wartością zadaną dla regulatorów P, praz podana na elementy wykonawcze2/Sum4:1
LINE Moduł sprawdzający czy wpisana pozycja dla ruchu, może być wartością zadaną dla regulatorów P, praz podana na elementy wykonawcze2/os4:1 -> Moduł sprawdzający czy wpisana pozycja dla ruchu, może być wartością zadaną dla regulatorów P, praz podana na elementy wykonawcze2/Sum5:1
LINE Moduł sprawdzający czy wpisana pozycja dla ruchu, może być wartością zadaną dla regulatorów P, praz podana na elementy wykonawcze2/os5:1 -> Moduł sprawdzający czy wpisana pozycja dla ruchu, może być wartością zadaną dla regulatorów P, praz podana na elementy wykonawcze2/Goto2:1
LINE Moduł sprawdzający czy wpisana pozycja dla ruchu, może być wartością zadaną dla regulatorów P, praz podana na elementy wykonawcze2/os5:1 -> Moduł sprawdzający czy wpisana pozycja dla ruchu, może być wartością zadaną dla regulatorów P, praz podana na elementy wykonawcze2/Sum6:1
LINE Moduł sprawdzający czy wpisana pozycja dla ruchu, może być wartością zadaną dla regulatorów P, praz podana na elementy wykonawcze2/os5:1 -> Moduł sprawdzający czy wpisana pozycja dla ruchu, może być wartością zadaną dla regulatorów P, praz podana na elementy wykonawcze2/Sum7:1
LINE Moduł sprawdzający czy wpisana pozycja dla ruchu, może być wartością zadaną dla regulatorów P, praz podana na elementy wykonawcze2:1 -> Data Store Write:1
LINE Moduł sprawdzający czy wpisana pozycja dla ruchu, może być wartością zadaną dla regulatorów P, praz podana na elementy wykonawcze2:2 -> Data Store Write1:1
LINE Moduł sprawdzający czy wpisana pozycja dla ruchu, może być wartością zadaną dla regulatorów P, praz podana na elementy wykonawcze2:3 -> Data Store Write2:1
LINE Moduł sprawdzający czy wpisana pozycja dla ruchu, może być wartością zadaną dla regulatorów P, praz podana na elementy wykonawcze2:4 -> Data Store Write3:1
LINE Moduł sprawdzający czy wpisana pozycja dla ruchu, może być wartością zadaną dla regulatorów P, praz podana na elementy wykonawcze2:5 -> Data Store Write4:1
LINE Position 1/Filters 1/Analog Butterworth LP Filter/Analog Butterworth LP Filter:1 -> Position 1/Filters 1/Analog Butterworth LP Filter/Out1:1
LINE Position 1/Filters 1/Analog Butterworth LP Filter/In1:1 -> Position 1/Filters 1/Analog Butterworth LP Filter/Analog Butterworth LP Filter:1
LINE Position 1/Filters 1/Analog Butterworth LP Filter1/Analog Butterworth LP Filter1:1 -> Position 1/Filters 1/Analog Butterworth LP Filter1/Out1:1
LINE Position 1/Filters 1/Analog Butterworth LP Filter1/In1:1 -> Position 1/Filters 1/Analog Butterworth LP Filter1/Analog Butterworth LP Filter1:1
LINE Position 1/Filters 1/Analog Butterworth LP Filter1:1 -> Position 1/Filters 1/Cos:1
LINE Position 1/Filters 1/Analog Butterworth LP Filter:1 -> Position 1/Filters 1/Sin:1
LINE Position 1/Filters 1/Demux:1 -> Position 1/Filters 1/Analog Butterworth LP Filter:1
LINE Position 1/Filters 1/Demux:2 -> Position 1/Filters 1/Analog Butterworth LP Filter1:1
LINE Position 1/Filters 1/Sin && Cos:1 -> Position 1/Filters 1/Demux:1
LINE Position 1/Filters 1:1 -> Position 1/Position Calculation 1:1
LINE Position 1/Filters 1:2 -> Position 1/Position Calculation 1:2
LINE Position 1/Position Calculation 1/Atan2:1 -> Position 1/Position Calculation 1/Derivative:1
LINE Position 1/Position Calculation 1/Atan2:1 -> Position 1/Position Calculation 1/Init Angle:3
LINE Position 1/Position Calculation 1/Atan2:1 -> Position 1/Position Calculation 1/Sum1:2
LINE Position 1/Position Calculation 1/Conversion Rad to Deg:1 -> Position 1/Position Calculation 1/Position:1
LINE Position 1/Position Calculation 1/Conversion Rotation to Angle:1 -> Position 1/Position Calculation 1/Sum1:1
LINE Position 1/Position Calculation 1/Cos:1 -> Position 1/Position Calculation 1/Mux:2
LINE Position 1/Position Calculation 1/Dead Zone:1 -> Position 1/Position Calculation 1/Saturation:1
LINE Position 1/Position Calculation 1/Derivative:1 -> Position 1/Position Calculation 1/Dead Zone:1
LINE Position 1/Position Calculation 1/Gear:1 -> Position 1/Position Calculation 1/Conversion Rad to Deg:1
LINE Position 1/Position Calculation 1/Init Angle:1 -> Position 1/Position Calculation 1/Memory1:1
LINE Position 1/Position Calculation 1/Init Angle:1 -> Position 1/Position Calculation 1/Sum1:3
LINE Position 1/Position Calculation 1/Memory1:1 -> Position 1/Position Calculation 1/Init Angle:1
LINE Position 1/Position Calculation 1/Memory:1 -> Position 1/Position Calculation 1/Sum:1
LINE Position 1/Position Calculation 1/Mux:1 -> Position 1/Position Calculation 1/Atan2:1
LINE Position 1/Position Calculation 1/Product:1 -> Position 1/Position Calculation 1/Conversion Rotation to Angle:1
LINE Position 1/Position Calculation 1/Product:1 -> Position 1/Position Calculation 1/Memory:1
LINE Position 1/Position Calculation 1/Reset (Impulse):1 -> Position 1/Position Calculation 1/Init Angle:2
LINE Position 1/Position Calculation 1/Reset (Impulse):1 -> Position 1/Position Calculation 1/Product:2
LINE Position 1/Position Calculation 1/Saturation:1 -> Position 1/Position Calculation 1/Sum:2
LINE Position 1/Position Calculation 1/Sin:1 -> Position 1/Position Calculation 1/Mux:1
LINE Position 1/Position Calculation 1/Sum1:1 -> Position 1/Position Calculation 1/Gear:1
LINE Position 1/Position Calculation 1/Sum:1 -> Position 1/Position Calculation 1/Product:1
LINE Position 1/Position Calculation 1:1 -> Position 1/Out1:1
LINE Position 1/Reset 1:1 -> Position 1/Position Calculation 1:3
LINE Position 1/Sin && Cos1:1 -> Position 1/Filters 1:1
LINE Position 1:1 -> Goto:1
LINE Position 2/Filters 2/Analog Butterworth LP Filter/Analog Butterworth LP Filter:1 -> Position 2/Filters 2/Analog Butterworth LP Filter/Out1:1
LINE Position 2/Filters 2/Analog Butterworth LP Filter/In1:1 -> Position 2/Filters 2/Analog Butterworth LP Filter/Analog Butterworth LP Filter:1
LINE Position 2/Filters 2/Analog Butterworth LP Filter1/Analog Butterworth LP Filter1:1 -> Position 2/Filters 2/Analog Butterworth LP Filter1/Out1:1
LINE Position 2/Filters 2/Analog Butterworth LP Filter1/In1:1 -> Position 2/Filters 2/Analog Butterworth LP Filter1/Analog Butterworth LP Filter1:1
LINE Position 2/Filters 2/Analog Butterworth LP Filter1:1 -> Position 2/Filters 2/Cos:1
LINE Position 2/Filters 2/Analog Butterworth LP Filter:1 -> Position 2/Filters 2/Sin:1
LINE Position 2/Filters 2/Demux:1 -> Position 2/Filters 2/Analog Butterworth LP Filter:1
LINE Position 2/Filters 2/Demux:2 -> Position 2/Filters 2/Analog Butterworth LP Filter1:1
LINE Position 2/Filters 2/Sin && Cos:1 -> Position 2/Filters 2/Demux:1
LINE Position 2/Filters 2:1 -> Position 2/Position Calculation 2:1
LINE Position 2/Filters 2:2 -> Position 2/Position Calculation 2:2
LINE Position 2/Position Calculation 2/Atan2:1 -> Position 2/Position Calculation 2/Derivative:1
LINE Position 2/Position Calculation 2/Atan2:1 -> Position 2/Position Calculation 2/Init Angle:3
LINE Position 2/Position Calculation 2/Atan2:1 -> Position 2/Position Calculation 2/Sum1:2
LINE Position 2/Position Calculation 2/Conversion Rad to Deg:1 -> Position 2/Position Calculation 2/Position:1
LINE Position 2/Position Calculation 2/Conversion Rotation to Angle:1 -> Position 2/Position Calculation 2/Sum1:1
LINE Position 2/Position Calculation 2/Cos:1 -> Position 2/Position Calculation 2/Mux:2
LINE Position 2/Position Calculation 2/Dead Zone:1 -> Position 2/Position Calculation 2/Saturation:1
LINE Position 2/Position Calculation 2/Derivative:1 -> Position 2/Position Calculation 2/Dead Zone:1
LINE Position 2/Position Calculation 2/Gear:1 -> Position 2/Position Calculation 2/Conversion Rad to Deg:1
LINE Position 2/Position Calculation 2/Init Angle:1 -> Position 2/Position Calculation 2/Memory1:1
LINE Position 2/Position Calculation 2/Init Angle:1 -> Position 2/Position Calculation 2/Sum1:3
LINE Position 2/Position Calculation 2/Memory1:1 -> Position 2/Position Calculation 2/Init Angle:1
LINE Position 2/Position Calculation 2/Memory:1 -> Position 2/Position Calculation 2/Sum:1
LINE Position 2/Position Calculation 2/Mux:1 -> Position 2/Position Calculation 2/Atan2:1
LINE Position 2/Position Calculation 2/Product:1 -> Position 2/Position Calculation 2/Conversion Rotation to Angle:1
LINE Position 2/Position Calculation 2/Product:1 -> Position 2/Position Calculation 2/Memory:1
LINE Position 2/Position Calculation 2/Reset (Impulse):1 -> Position 2/Position Calculation 2/Init Angle:2
LINE Position 2/Position Calculation 2/Reset (Impulse):1 -> Position 2/Position Calculation 2/Product:2
LINE Position 2/Position Calculation 2/Saturation:1 -> Position 2/Position Calculation 2/Sum:2
LINE Position 2/Position Calculation 2/Sin:1 -> Position 2/Position Calculation 2/Mux:1
LINE Position 2/Position Calculation 2/Sum1:1 -> Position 2/Position Calculation 2/Gear:1
LINE Position 2/Position Calculation 2/Sum:1 -> Position 2/Position Calculation 2/Product:1
LINE Position 2/Position Calculation 2:1 -> Position 2/Out1:1
LINE Position 2/Reset 2:1 -> Position 2/Position Calculation 2:3
LINE Position 2/Sin && Cos2:1 -> Position 2/Filters 2:1
LINE Position 2:1 -> Goto1:1
LINE Position 3/Filters 3/Analog Butterworth LP Filter/Analog Butterworth LP Filter:1 -> Position 3/Filters 3/Analog Butterworth LP Filter/Out1:1
LINE Position 3/Filters 3/Analog Butterworth LP Filter/In1:1 -> Position 3/Filters 3/Analog Butterworth LP Filter/Analog Butterworth LP Filter:1
LINE Position 3/Filters 3/Analog Butterworth LP Filter1/Analog Butterworth LP Filter1:1 -> Position 3/Filters 3/Analog Butterworth LP Filter1/Out1:1
LINE Position 3/Filters 3/Analog Butterworth LP Filter1/In1:1 -> Position 3/Filters 3/Analog Butterworth LP Filter1/Analog Butterworth LP Filter1:1
LINE Position 3/Filters 3/Analog Butterworth LP Filter1:1 -> Position 3/Filters 3/Cos:1
LINE Position 3/Filters 3/Analog Butterworth LP Filter:1 -> Position 3/Filters 3/Sin:1
LINE Position 3/Filters 3/Demux:1 -> Position 3/Filters 3/Analog Butterworth LP Filter:1
LINE Position 3/Filters 3/Demux:2 -> Position 3/Filters 3/Analog Butterworth LP Filter1:1
LINE Position 3/Filters 3/Sin && Cos:1 -> Position 3/Filters 3/Demux:1
LINE Position 3/Filters 3:1 -> Position 3/Position Calculation 3:1
LINE Position 3/Filters 3:2 -> Position 3/Position Calculation 3:2
LINE Position 3/Position Calculation 3/Atan2:1 -> Position 3/Position Calculation 3/Derivative:1
LINE Position 3/Position Calculation 3/Atan2:1 -> Position 3/Position Calculation 3/Init Angle:3
LINE Position 3/Position Calculation 3/Atan2:1 -> Position 3/Position Calculation 3/Sum1:2
LINE Position 3/Position Calculation 3/Conversion Rad to Deg:1 -> Position 3/Position Calculation 3/Position:1
LINE Position 3/Position Calculation 3/Conversion Rotation to Angle:1 -> Position 3/Position Calculation 3/Sum1:1
LINE Position 3/Position Calculation 3/Cos:1 -> Position 3/Position Calculation 3/Mux:2
LINE Position 3/Position Calculation 3/Dead Zone:1 -> Position 3/Position Calculation 3/Saturation:1
LINE Position 3/Position Calculation 3/Derivative:1 -> Position 3/Position Calculation 3/Dead Zone:1
LINE Position 3/Position Calculation 3/Gear:1 -> Position 3/Position Calculation 3/Conversion Rad to Deg:1
LINE Position 3/Position Calculation 3/Init Angle:1 -> Position 3/Position Calculation 3/Memory1:1
LINE Position 3/Position Calculation 3/Init Angle:1 -> Position 3/Position Calculation 3/Sum1:3
LINE Position 3/Position Calculation 3/Memory1:1 -> Position 3/Position Calculation 3/Init Angle:1
LINE Position 3/Position Calculation 3/Memory:1 -> Position 3/Position Calculation 3/Sum:1
LINE Position 3/Position Calculation 3/Mux:1 -> Position 3/Position Calculation 3/Atan2:1
LINE Position 3/Position Calculation 3/Product:1 -> Position 3/Position Calculation 3/Conversion Rotation to Angle:1
LINE Position 3/Position Calculation 3/Product:1 -> Position 3/Position Calculation 3/Memory:1
LINE Position 3/Position Calculation 3/Reset (Impulse):1 -> Position 3/Position Calculation 3/Init Angle:2
LINE Position 3/Position Calculation 3/Reset (Impulse):1 -> Position 3/Position Calculation 3/Product:2
LINE Position 3/Position Calculation 3/Saturation:1 -> Position 3/Position Calculation 3/Sum:2
LINE Position 3/Position Calculation 3/Sin:1 -> Position 3/Position Calculation 3/Mux:1
LINE Position 3/Position Calculation 3/Sum1:1 -> Position 3/Position Calculation 3/Gear:1
LINE Position 3/Position Calculation 3/Sum:1 -> Position 3/Position Calculation 3/Product:1
LINE Position 3/Position Calculation 3:1 -> Position 3/Out1:1
LINE Position 3/Reset 3:1 -> Position 3/Position Calculation 3:3
LINE Position 3/Sin && Cos3:1 -> Position 3/Filters 3:1
LINE Position 3:1 -> Goto2:1
LINE Position 4/Filters 4/Analog Butterworth LP Filter/Analog Butterworth LP Filter:1 -> Position 4/Filters 4/Analog Butterworth LP Filter/Out1:1
LINE Position 4/Filters 4/Analog Butterworth LP Filter/In1:1 -> Position 4/Filters 4/Analog Butterworth LP Filter/Analog Butterworth LP Filter:1
LINE Position 4/Filters 4/Analog Butterworth LP Filter1/Analog Butterworth LP Filter1:1 -> Position 4/Filters 4/Analog Butterworth LP Filter1/Out1:1
LINE Position 4/Filters 4/Analog Butterworth LP Filter1/In1:1 -> Position 4/Filters 4/Analog Butterworth LP Filter1/Analog Butterworth LP Filter1:1
LINE Position 4/Filters 4/Analog Butterworth LP Filter1:1 -> Position 4/Filters 4/Cos:1
LINE Position 4/Filters 4/Analog Butterworth LP Filter:1 -> Position 4/Filters 4/Sin:1
LINE Position 4/Filters 4/Demux:1 -> Position 4/Filters 4/Analog Butterworth LP Filter:1
LINE Position 4/Filters 4/Demux:2 -> Position 4/Filters 4/Analog Butterworth LP Filter1:1
LINE Position 4/Filters 4/Sin && Cos:1 -> Position 4/Filters 4/Demux:1
LINE Position 4/Filters 4:1 -> Position 4/Position Calculation 4:1
LINE Position 4/Filters 4:2 -> Position 4/Position Calculation 4:2
LINE Position 4/Position Calculation 4/Atan2:1 -> Position 4/Position Calculation 4/Derivative:1
LINE Position 4/Position Calculation 4/Atan2:1 -> Position 4/Position Calculation 4/Init Angle:3
LINE Position 4/Position Calculation 4/Atan2:1 -> Position 4/Position Calculation 4/Sum1:2
LINE Position 4/Position Calculation 4/Conversion Rad to Deg:1 -> Position 4/Position Calculation 4/Position:1
LINE Position 4/Position Calculation 4/Conversion Rotation to Angle:1 -> Position 4/Position Calculation 4/Sum1:1
LINE Position 4/Position Calculation 4/Cos:1 -> Position 4/Position Calculation 4/Mux:2
LINE Position 4/Position Calculation 4/Dead Zone:1 -> Position 4/Position Calculation 4/Saturation:1
LINE Position 4/Position Calculation 4/Derivative:1 -> Position 4/Position Calculation 4/Dead Zone:1
LINE Position 4/Position Calculation 4/Gear:1 -> Position 4/Position Calculation 4/Conversion Rad to Deg:1
LINE Position 4/Position Calculation 4/Init Angle:1 -> Position 4/Position Calculation 4/Memory1:1
LINE Position 4/Position Calculation 4/Init Angle:1 -> Position 4/Position Calculation 4/Sum1:3
LINE Position 4/Position Calculation 4/Memory1:1 -> Position 4/Position Calculation 4/Init Angle:1
LINE Position 4/Position Calculation 4/Memory:1 -> Position 4/Position Calculation 4/Sum:1
LINE Position 4/Position Calculation 4/Mux:1 -> Position 4/Position Calculation 4/Atan2:1
LINE Position 4/Position Calculation 4/Product:1 -> Position 4/Position Calculation 4/Conversion Rotation to Angle:1
LINE Position 4/Position Calculation 4/Product:1 -> Position 4/Position Calculation 4/Memory:1
LINE Position 4/Position Calculation 4/Reset (Impulse):1 -> Position 4/Position Calculation 4/Init Angle:2
LINE Position 4/Position Calculation 4/Reset (Impulse):1 -> Position 4/Position Calculation 4/Product:2
LINE Position 4/Position Calculation 4/Saturation:1 -> Position 4/Position Calculation 4/Sum:2
LINE Position 4/Position Calculation 4/Sin:1 -> Position 4/Position Calculation 4/Mux:1
LINE Position 4/Position Calculation 4/Sum1:1 -> Position 4/Position Calculation 4/Gear:1
LINE Position 4/Position Calculation 4/Sum:1 -> Position 4/Position Calculation 4/Product:1
LINE Position 4/Position Calculation 4:1 -> Position 4/Out1:1
LINE Position 4/Reset 4:1 -> Position 4/Position Calculation 4:3
LINE Position 4/Sin && Cos4:1 -> Position 4/Filters 4:1
LINE Position 4:1 -> Goto3:1
LINE Position 5/Filters 5/Analog Butterworth LP Filter/Analog Butterworth LP Filter:1 -> Position 5/Filters 5/Analog Butterworth LP Filter/Out1:1
LINE Position 5/Filters 5/Analog Butterworth LP Filter/In1:1 -> Position 5/Filters 5/Analog Butterworth LP Filter/Analog Butterworth LP Filter:1
LINE Position 5/Filters 5/Analog Butterworth LP Filter1/Analog Butterworth LP Filter1:1 -> Position 5/Filters 5/Analog Butterworth LP Filter1/Out1:1
LINE Position 5/Filters 5/Analog Butterworth LP Filter1/In1:1 -> Position 5/Filters 5/Analog Butterworth LP Filter1/Analog Butterworth LP Filter1:1
LINE Position 5/Filters 5/Analog Butterworth LP Filter1:1 -> Position 5/Filters 5/Cos:1
LINE Position 5/Filters 5/Analog Butterworth LP Filter:1 -> Position 5/Filters 5/Sin:1
LINE Position 5/Filters 5/Demux:1 -> Position 5/Filters 5/Analog Butterworth LP Filter:1
LINE Position 5/Filters 5/Demux:2 -> Position 5/Filters 5/Analog Butterworth LP Filter1:1
LINE Position 5/Filters 5/Sin && Cos:1 -> Position 5/Filters 5/Demux:1
LINE Position 5/Filters 5:1 -> Position 5/Position Calculation 5:1
LINE Position 5/Filters 5:2 -> Position 5/Position Calculation 5:2
LINE Position 5/Position Calculation 5/Atan2:1 -> Position 5/Position Calculation 5/Derivative:1
LINE Position 5/Position Calculation 5/Atan2:1 -> Position 5/Position Calculation 5/Init Angle:3
LINE Position 5/Position Calculation 5/Atan2:1 -> Position 5/Position Calculation 5/Sum1:2
LINE Position 5/Position Calculation 5/Conversion Rad to Deg:1 -> Position 5/Position Calculation 5/Position:1
LINE Position 5/Position Calculation 5/Conversion Rotation to Angle:1 -> Position 5/Position Calculation 5/Sum1:1
LINE Position 5/Position Calculation 5/Cos:1 -> Position 5/Position Calculation 5/Mux:2
LINE Position 5/Position Calculation 5/Dead Zone:1 -> Position 5/Position Calculation 5/Saturation:1
LINE Position 5/Position Calculation 5/Derivative:1 -> Position 5/Position Calculation 5/Dead Zone:1
LINE Position 5/Position Calculation 5/Gear:1 -> Position 5/Position Calculation 5/Conversion Rad to Deg:1
LINE Position 5/Position Calculation 5/Init Angle:1 -> Position 5/Position Calculation 5/Memory1:1
LINE Position 5/Position Calculation 5/Init Angle:1 -> Position 5/Position Calculation 5/Sum1:3
LINE Position 5/Position Calculation 5/Memory1:1 -> Position 5/Position Calculation 5/Init Angle:1
LINE Position 5/Position Calculation 5/Memory:1 -> Position 5/Position Calculation 5/Sum:1
LINE Position 5/Position Calculation 5/Mux:1 -> Position 5/Position Calculation 5/Atan2:1
LINE Position 5/Position Calculation 5/Product:1 -> Position 5/Position Calculation 5/Conversion Rotation to Angle:1
LINE Position 5/Position Calculation 5/Product:1 -> Position 5/Position Calculation 5/Memory:1
LINE Position 5/Position Calculation 5/Reset (Impulse):1 -> Position 5/Position Calculation 5/Init Angle:2
LINE Position 5/Position Calculation 5/Reset (Impulse):1 -> Position 5/Position Calculation 5/Product:2
LINE Position 5/Position Calculation 5/Saturation:1 -> Position 5/Position Calculation 5/Sum:2
LINE Position 5/Position Calculation 5/Sin:1 -> Position 5/Position Calculation 5/Mux:1
LINE Position 5/Position Calculation 5/Sum1:1 -> Position 5/Position Calculation 5/Gear:1
LINE Position 5/Position Calculation 5/Sum:1 -> Position 5/Position Calculation 5/Product:1
LINE Position 5/Position Calculation 5:1 -> Position 5/Out1:1
LINE Position 5/Reset 5:1 -> Position 5/Position Calculation 5:3
LINE Position 5/Sin && Cos5:1 -> Position 5/Filters 5:1
LINE Position 5:1 -> Goto4:1
LINE Regulator P/Constant1:1 -> Regulator P/Switch1:1
LINE Regulator P/Constant:1 -> Regulator P/Switch:1
LINE Regulator P/Data Store Read10:1 -> Regulator P/Logical Operator:1
LINE Regulator P/Data Store Read11:1 -> Regulator P/S-R Flip-Flop:1
LINE Regulator P/Data Store Read12:1 -> Regulator P/Logical Operator:2
LINE Regulator P/Data Store Read16:1 -> Regulator P/Product:2
LINE Regulator P/Gain1:1 -> Regulator P/sterowanie:1
LINE Regulator P/Gain:1 -> Regulator P/Saturation:1
LINE Regulator P/Logical Operator:1 -> Regulator P/S-R Flip-Flop:2
LINE Regulator P/Product:1 -> Regulator P/Switch:3
LINE Regulator P/Rate Limiter:1 -> Regulator P/Gain1:1
LINE Regulator P/S-R Flip-Flop:1 -> Regulator P/Switch1:2
LINE Regulator P/S-R Flip-Flop:1 -> Regulator P/Switch:2
LINE Regulator P/S-R Flip-Flop:2 -> Regulator P/Data Store Write8:1
LINE Regulator P/Saturation:1 -> Regulator P/Product:1
LINE Regulator P/Sum:1 -> Regulator P/Gain:1
LINE Regulator P/Switch1:1 -> Regulator P/Data Store Write1:1
LINE Regulator P/Switch:1 -> Regulator P/Rate Limiter:1
LINE Regulator P/pomiar :1 -> Regulator P/Sum:2
LINE Regulator P/zadana:1 -> Regulator P/Sum:1
LINE Regulator P/zadana:1 -> Regulator P/Switch1:3
LINE Regulator P1/Constant1:1 -> Regulator P1/Switch1:1
LINE Regulator P1/Constant:1 -> Regulator P1/Switch:1
LINE Regulator P1/Data Store Read10:1 -> Regulator P1/Logical Operator:1
LINE Regulator P1/Data Store Read11:1 -> Regulator P1/S-R Flip-Flop:1
LINE Regulator P1/Data Store Read12:1 -> Regulator P1/Logical Operator:2
LINE Regulator P1/Data Store Read16:1 -> Regulator P1/Product:2
LINE Regulator P1/Gain1:1 -> Regulator P1/sterowanie:1
LINE Regulator P1/Gain:1 -> Regulator P1/Saturation:1
LINE Regulator P1/Logical Operator:1 -> Regulator P1/S-R Flip-Flop:2
LINE Regulator P1/Product:1 -> Regulator P1/Switch:3
LINE Regulator P1/Rate Limiter:1 -> Regulator P1/Gain1:1
LINE Regulator P1/S-R Flip-Flop:1 -> Regulator P1/Switch1:2
LINE Regulator P1/S-R Flip-Flop:1 -> Regulator P1/Switch:2
LINE Regulator P1/S-R Flip-Flop:2 -> Regulator P1/Data Store Write8:1
LINE Regulator P1/Saturation:1 -> Regulator P1/Product:1
LINE Regulator P1/Sum:1 -> Regulator P1/Gain:1
LINE Regulator P1/Switch1:1 -> Regulator P1/Data Store Write1:1
LINE Regulator P1/Switch:1 -> Regulator P1/Rate Limiter:1
LINE Regulator P1/pomiar :1 -> Regulator P1/Sum:2
LINE Regulator P1/zadana:1 -> Regulator P1/Sum:1
LINE Regulator P1/zadana:1 -> Regulator P1/Switch1:3
LINE Regulator P1:1 -> DS2201DAC_B1:1
LINE Regulator P2/Data Store Read16:1 -> Regulator P2/Product:2
LINE Regulator P2/Gain1:1 -> Regulator P2/sterowanie:1
LINE Regulator P2/Gain:1 -> Regulator P2/Saturation:1
LINE Regulator P2/Product:1 -> Regulator P2/Rate Limiter:1
LINE Regulator P2/Rate Limiter:1 -> Regulator P2/Gain1:1
LINE Regulator P2/Saturation:1 -> Regulator P2/Product:1
LINE Regulator P2/Sum:1 -> Regulator P2/Gain:1
LINE Regulator P2/pomiar :1 -> Regulator P2/Sum:2
LINE Regulator P2/zadana:1 -> Regulator P2/Sum:1
LINE Regulator P2:1 -> DS2201DAC_B1:4
LINE Regulator P3/Constant1:1 -> Regulator P3/Switch1:1
LINE Regulator P3/Constant:1 -> Regulator P3/Switch:1
LINE Regulator P3/Data Store Read10:1 -> Regulator P3/Logical Operator:1
LINE Regulator P3/Data Store Read11:1 -> Regulator P3/S-R Flip-Flop:1
LINE Regulator P3/Data Store Read12:1 -> Regulator P3/Logical Operator:2
LINE Regulator P3/Data Store Read16:1 -> Regulator P3/Product:2
LINE Regulator P3/Gain2:1 -> Regulator P3/Saturation1:1
LINE Regulator P3/Gain3:1 -> Regulator P3/sterowanie:1
LINE Regulator P3/Logical Operator:1 -> Regulator P3/S-R Flip-Flop:2
LINE Regulator P3/Product:1 -> Regulator P3/Switch:3
LINE Regulator P3/Rate Limiter1:1 -> Regulator P3/Gain3:1
LINE Regulator P3/S-R Flip-Flop:1 -> Regulator P3/Switch1:2
LINE Regulator P3/S-R Flip-Flop:1 -> Regulator P3/Switch:2
LINE Regulator P3/S-R Flip-Flop:2 -> Regulator P3/Data Store Write8:1
LINE Regulator P3/Saturation1:1 -> Regulator P3/Product:1
LINE Regulator P3/Sum1:1 -> Regulator P3/Gain2:1
LINE Regulator P3/Switch1:1 -> Regulator P3/Data Store Write1:1
LINE Regulator P3/Switch:1 -> Regulator P3/Rate Limiter1:1
LINE Regulator P3/pomiar 2:1 -> Regulator P3/Sum1:2
LINE Regulator P3/zadana:1 -> Regulator P3/Sum1:1
LINE Regulator P3/zadana:1 -> Regulator P3/Switch1:3
LINE Regulator P3:1 -> DS2201DAC_B1:3
LINE Regulator P4/Data Store Read16:1 -> Regulator P4/Product:2
LINE Regulator P4/Gain1:1 -> Regulator P4/sterowanie:1
LINE Regulator P4/Gain:1 -> Regulator P4/Saturation:1
LINE Regulator P4/Product:1 -> Regulator P4/Rate Limiter:1
LINE Regulator P4/Rate Limiter:1 -> Regulator P4/Gain1:1
LINE Regulator P4/Saturation:1 -> Regulator P4/Product:1
LINE Regulator P4/Sum:1 -> Regulator P4/Gain:1
LINE Regulator P4/pomiar :1 -> Regulator P4/Sum:2
LINE Regulator P4/zadana:1 -> Regulator P4/Sum:1
LINE Regulator P4:1 -> DS2201DAC_B1:5
LINE Regulator P:1 -> DS2201DAC_B1:2
LINE Saturation:1 -> Gain:1
LINE os4_reset:1 -> Position 4:2
LINE os5_reset :1 -> Position 5:2
